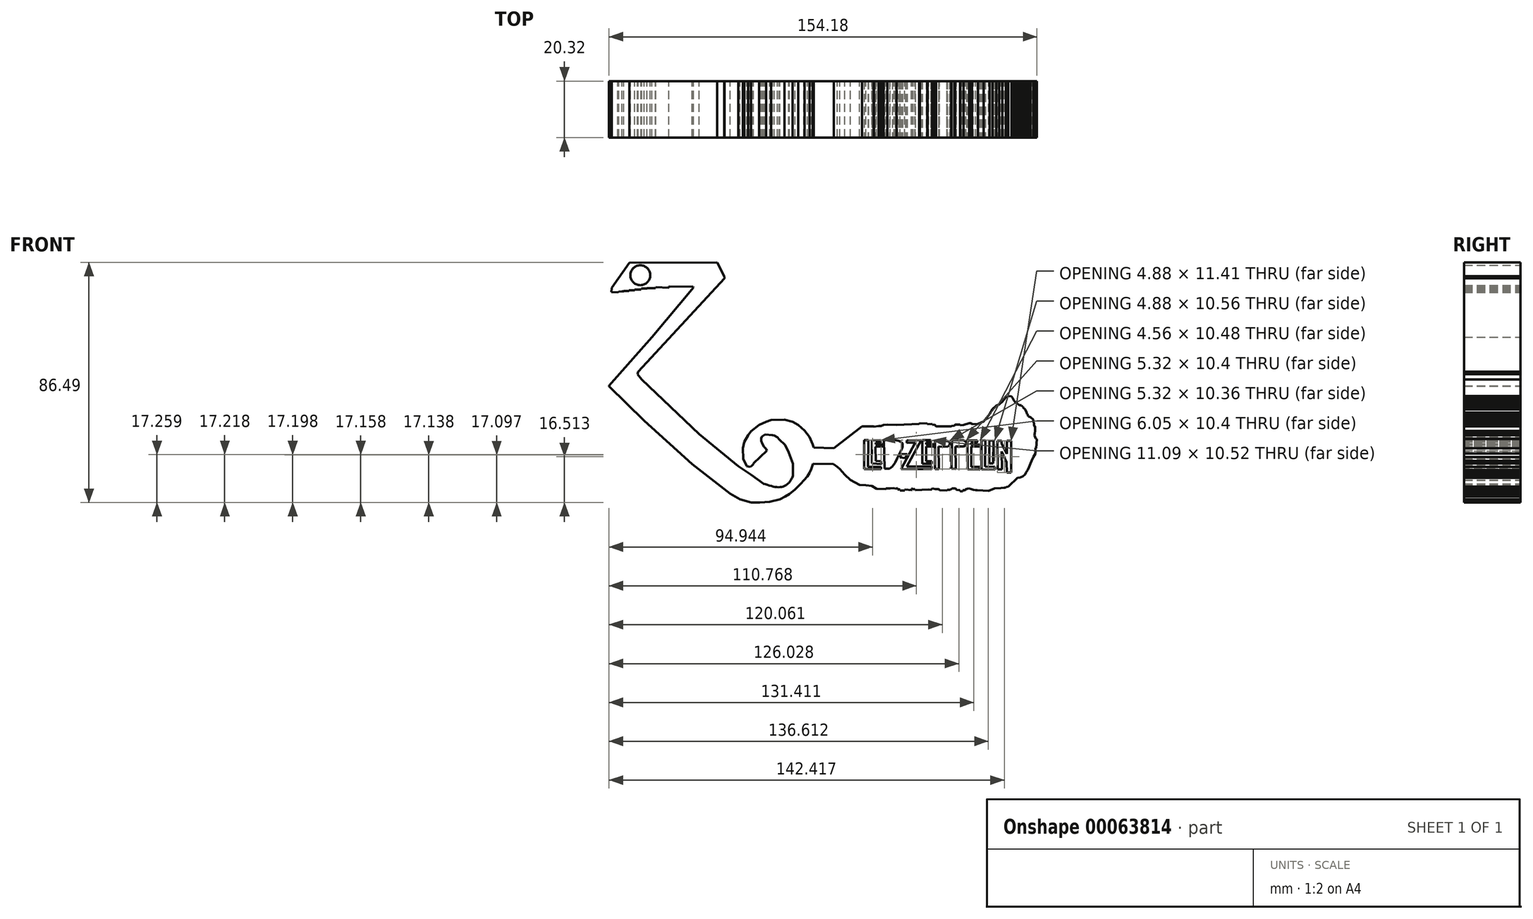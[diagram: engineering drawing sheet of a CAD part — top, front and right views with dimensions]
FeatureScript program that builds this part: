
annotation { "Feature Type Name" : "Feature", "Feature Type Description" : "" }
export const myFeature = defineFeature(function(context is Context, id is Id, definition is map)
    precondition{}
    {
        {
            var Q0;
            Q0=qCreatedBy(makeId("Front.planeOp"),FACE);
            var sketch = newSketch(context, id + "F0", { "sketchPlane" : qUnion([Q0])});
            skLineSegment(sketch, "E0", {"start": v(-87.17, 53.85) * mm, "end": v(-47.68, 54.06) * mm});
            skLineSegment(sketch, "E1", {"start": v(-47.68, 54.06) * mm, "end": v(-44.47, 47.79) * mm});
            skLineSegment(sketch, "E2", {"start": v(-44.47, 47.79) * mm, "end": v(-44.33, 46.86) * mm});
            skLineSegment(sketch, "E3", {"start": v(-44.33, 46.86) * mm, "end": v(-83.17, 4.81) * mm});
            skLineSegment(sketch, "E4", {"start": v(-83.17, 4.81) * mm, "end": v(-83.6, 3.74) * mm});
            skLineSegment(sketch, "E5", {"start": v(-83.6, 3.74) * mm, "end": v(-81.6, 1.39) * mm});
            skLineSegment(sketch, "E6", {"start": v(-81.6, 1.39) * mm, "end": v(-55.8, -23.34) * mm});
            skLineSegment(sketch, "E7", {"start": v(-55.8, -23.34) * mm, "end": v(-38.13, -37.67) * mm});
            skLineSegment(sketch, "E8", {"start": v(-38.13, -37.67) * mm, "end": v(-32.5, -41.52) * mm});
            skLineSegment(sketch, "E9", {"start": v(-32.5, -41.52) * mm, "end": v(-26.73, -45.58) * mm});
            skLineSegment(sketch, "E10", {"start": v(-13.61, -36.67) * mm, "end": v(-15.4, -31.47) * mm});
            skLineSegment(sketch, "E11", {"start": v(-19.67, -25.7) * mm, "end": v(-20.6, -24.77) * mm});
            skLineSegment(sketch, "E12", {"start": v(-20.6, -24.77) * mm, "end": v(-21.95, -23.91) * mm});
            skLineSegment(sketch, "E13", {"start": v(-21.95, -23.91) * mm, "end": v(-22.74, -23.7) * mm});
            skLineSegment(sketch, "E14", {"start": v(-22.74, -23.7) * mm, "end": v(-26.16, -23.41) * mm});
            skLineSegment(sketch, "E15", {"start": v(-26.16, -23.41) * mm, "end": v(-27.44, -24.34) * mm});
            skLineSegment(sketch, "E16", {"start": v(-27.44, -24.34) * mm, "end": v(-27.8, -25.12) * mm});
            skLineSegment(sketch, "E17", {"start": v(-27.8, -25.12) * mm, "end": v(-27.87, -26.33) * mm});
            skLineSegment(sketch, "E18", {"start": v(-27.87, -26.33) * mm, "end": v(-27.37, -27.62) * mm});
            skLineSegment(sketch, "E19", {"start": v(-27.37, -27.62) * mm, "end": v(-26.58, -28.9) * mm});
            skLineSegment(sketch, "E20", {"start": v(-26.58, -28.9) * mm, "end": v(-25.59, -29.9) * mm});
            skLineSegment(sketch, "E21", {"start": v(-25.59, -29.9) * mm, "end": v(-25.23, -30.75) * mm});
            skLineSegment(sketch, "E22", {"start": v(-25.23, -30.75) * mm, "end": v(-31.29, -36.38) * mm});
            skLineSegment(sketch, "E23", {"start": v(-31.29, -36.38) * mm, "end": v(-31.36, -36.81) * mm});
            skLineSegment(sketch, "E24", {"start": v(-31.36, -36.81) * mm, "end": v(-32, -37.45) * mm});
            skLineSegment(sketch, "E25", {"start": v(-32, -37.45) * mm, "end": v(-32.79, -37.95) * mm});
            skLineSegment(sketch, "E26", {"start": v(-32.79, -37.95) * mm, "end": v(-34.28, -37.67) * mm});
            skLineSegment(sketch, "E27", {"start": v(-34.28, -37.67) * mm, "end": v(-35.85, -34.32) * mm});
            skLineSegment(sketch, "E28", {"start": v(-35.85, -34.32) * mm, "end": v(-36.06, -29.68) * mm});
            skLineSegment(sketch, "E29", {"start": v(-36.06, -29.68) * mm, "end": v(-35.5, -26.83) * mm});
            skLineSegment(sketch, "E30", {"start": v(-35.5, -26.83) * mm, "end": v(-33.78, -23.77) * mm});
            skLineSegment(sketch, "E31", {"start": v(-33.78, -23.77) * mm, "end": v(-32.5, -22.06) * mm});
            skLineSegment(sketch, "E32", {"start": v(-32.5, -22.06) * mm, "end": v(-28.8, -19.07) * mm});
            skLineSegment(sketch, "E33", {"start": v(-28.8, -19.07) * mm, "end": v(-25.66, -17.64) * mm});
            skLineSegment(sketch, "E34", {"start": v(-25.66, -17.64) * mm, "end": v(-23.38, -16.86) * mm});
            skLineSegment(sketch, "E35", {"start": v(-23.38, -16.86) * mm, "end": v(-17.32, -16.71) * mm});
            skLineSegment(sketch, "E36", {"start": v(-17.32, -16.71) * mm, "end": v(-13.68, -17.78) * mm});
            skLineSegment(sketch, "E37", {"start": v(-13.68, -17.78) * mm, "end": v(-11.12, -19.2) * mm});
            skLineSegment(sketch, "E38", {"start": v(-11.12, -19.2) * mm, "end": v(-8.34, -21.63) * mm});
            skLineSegment(sketch, "E39", {"start": v(-8.34, -21.63) * mm, "end": v(-6.06, -24.55) * mm});
            skLineSegment(sketch, "E40", {"start": v(-6.06, -24.55) * mm, "end": v(-4.7, -27.83) * mm});
            skLineSegment(sketch, "E41", {"start": v(-4.7, -27.83) * mm, "end": v(-4.2, -29.33) * mm});
            skLineSegment(sketch, "E42", {"start": v(-4.2, -29.33) * mm, "end": v(4.92, -29.54) * mm});
            skLineSegment(sketch, "E43", {"start": v(4.92, -29.54) * mm, "end": v(17.53, -19.7) * mm});
            skLineSegment(sketch, "E44", {"start": v(17.53, -19.7) * mm, "end": v(22.88, -19.7) * mm});
            skLineSegment(sketch, "E45", {"start": v(22.88, -19.7) * mm, "end": v(23.02, -19.92) * mm});
            skLineSegment(sketch, "E46", {"start": v(23.02, -19.92) * mm, "end": v(25.02, -19.56) * mm});
            skLineSegment(sketch, "E47", {"start": v(25.02, -19.56) * mm, "end": v(26.09, -19.64) * mm});
            skLineSegment(sketch, "E48", {"start": v(26.09, -19.64) * mm, "end": v(27.3, -19.2) * mm});
            skLineSegment(sketch, "E49", {"start": v(27.3, -19.2) * mm, "end": v(28.94, -19) * mm});
            skLineSegment(sketch, "E50", {"start": v(28.94, -19) * mm, "end": v(33.07, -19.07) * mm});
            skLineSegment(sketch, "E51", {"start": v(33.07, -19.07) * mm, "end": v(43.33, -18.64) * mm});
            skLineSegment(sketch, "E52", {"start": v(43.33, -18.64) * mm, "end": v(43.62, -18.35) * mm});
            skLineSegment(sketch, "E53", {"start": v(43.62, -18.35) * mm, "end": v(46.9, -18.42) * mm});
            skLineSegment(sketch, "E54", {"start": v(46.9, -18.42) * mm, "end": v(47.11, -18.78) * mm});
            skLineSegment(sketch, "E55", {"start": v(47.11, -18.78) * mm, "end": v(49.18, -18.64) * mm});
            skLineSegment(sketch, "E56", {"start": v(49.18, -18.64) * mm, "end": v(49.32, -19.07) * mm});
            skLineSegment(sketch, "E57", {"start": v(49.32, -19.07) * mm, "end": v(50.25, -19) * mm});
            skLineSegment(sketch, "E58", {"start": v(50.25, -19) * mm, "end": v(50.96, -19.7) * mm});
            skLineSegment(sketch, "E59", {"start": v(50.96, -19.7) * mm, "end": v(57.8, -19.7) * mm});
            skLineSegment(sketch, "E60", {"start": v(57.8, -19.7) * mm, "end": v(57.94, -19.64) * mm});
            skLineSegment(sketch, "E61", {"start": v(57.94, -19.64) * mm, "end": v(59.23, -19.42) * mm});
            skLineSegment(sketch, "E62", {"start": v(59.23, -19.42) * mm, "end": v(59.51, -18.92) * mm});
            skLineSegment(sketch, "E63", {"start": v(59.51, -18.92) * mm, "end": v(61.65, -19) * mm});
            skLineSegment(sketch, "E64", {"start": v(61.65, -19) * mm, "end": v(61.94, -19.28) * mm});
            skLineSegment(sketch, "E65", {"start": v(61.94, -19.28) * mm, "end": v(63.29, -19.14) * mm});
            skLineSegment(sketch, "E66", {"start": v(63.29, -19.14) * mm, "end": v(65.78, -18.35) * mm});
            skLineSegment(sketch, "E67", {"start": v(65.78, -18.35) * mm, "end": v(66.85, -18.28) * mm});
            skLineSegment(sketch, "E68", {"start": v(66.85, -18.28) * mm, "end": v(67.07, -18.78) * mm});
            skLineSegment(sketch, "E69", {"start": v(67.07, -18.78) * mm, "end": v(69.78, -18.64) * mm});
            skLineSegment(sketch, "E70", {"start": v(69.78, -18.64) * mm, "end": v(72.34, -17.57) * mm});
            skLineSegment(sketch, "E71", {"start": v(72.34, -17.57) * mm, "end": v(75.05, -14.22) * mm});
            skLineSegment(sketch, "E72", {"start": v(75.05, -14.22) * mm, "end": v(76.26, -12) * mm});
            skLineSegment(sketch, "E73", {"start": v(76.26, -12) * mm, "end": v(78.11, -10.44) * mm});
            skLineSegment(sketch, "E74", {"start": v(78.11, -10.44) * mm, "end": v(79.4, -9.94) * mm});
            skLineSegment(sketch, "E75", {"start": v(79.4, -9.94) * mm, "end": v(80.68, -8.73) * mm});
            skLineSegment(sketch, "E76", {"start": v(80.68, -8.73) * mm, "end": v(82.4, -6.8) * mm});
            skLineSegment(sketch, "E77", {"start": v(82.4, -6.8) * mm, "end": v(83.03, -6.6) * mm});
            skLineSegment(sketch, "E78", {"start": v(83.03, -6.6) * mm, "end": v(83.46, -6.17) * mm});
            skLineSegment(sketch, "E79", {"start": v(83.46, -6.17) * mm, "end": v(84.81, -6.24) * mm});
            skLineSegment(sketch, "E80", {"start": v(84.81, -6.24) * mm, "end": v(85.31, -6.95) * mm});
            skLineSegment(sketch, "E81", {"start": v(85.31, -6.95) * mm, "end": v(85.74, -7.52) * mm});
            skLineSegment(sketch, "E82", {"start": v(85.74, -7.52) * mm, "end": v(85.95, -8.23) * mm});
            skLineSegment(sketch, "E83", {"start": v(85.95, -8.23) * mm, "end": v(86.45, -8.87) * mm});
            skLineSegment(sketch, "E84", {"start": v(86.45, -8.87) * mm, "end": v(87.24, -9.37) * mm});
            skLineSegment(sketch, "E85", {"start": v(87.24, -9.37) * mm, "end": v(88.38, -10.3) * mm});
            skLineSegment(sketch, "E86", {"start": v(88.38, -10.3) * mm, "end": v(89.3, -10.3) * mm});
            skLineSegment(sketch, "E87", {"start": v(89.3, -10.3) * mm, "end": v(89.59, -10.87) * mm});
            skLineSegment(sketch, "E88", {"start": v(89.59, -10.87) * mm, "end": v(90.09, -10.87) * mm});
            skLineSegment(sketch, "E89", {"start": v(90.09, -10.87) * mm, "end": v(90.16, -11.37) * mm});
            skLineSegment(sketch, "E90", {"start": v(90.16, -11.37) * mm, "end": v(91.01, -12.22) * mm});
            skLineSegment(sketch, "E91", {"start": v(91.01, -12.22) * mm, "end": v(91.51, -13.22) * mm});
            skLineSegment(sketch, "E92", {"start": v(91.51, -13.22) * mm, "end": v(91.73, -13.65) * mm});
            skLineSegment(sketch, "E93", {"start": v(91.73, -13.65) * mm, "end": v(91.8, -14.29) * mm});
            skLineSegment(sketch, "E94", {"start": v(91.8, -14.29) * mm, "end": v(92.15, -14.29) * mm});
            skLineSegment(sketch, "E95", {"start": v(92.15, -14.29) * mm, "end": v(92.15, -14.65) * mm});
            skLineSegment(sketch, "E96", {"start": v(92.15, -14.65) * mm, "end": v(92.44, -15.36) * mm});
            skLineSegment(sketch, "E97", {"start": v(94.65, -16.71) * mm, "end": v(94.8, -17.71) * mm});
            skLineSegment(sketch, "E98", {"start": v(94.8, -17.71) * mm, "end": v(95.08, -18.35) * mm});
            skLineSegment(sketch, "E99", {"start": v(95.08, -18.35) * mm, "end": v(95.08, -19.07) * mm});
            skLineSegment(sketch, "E100", {"start": v(95.08, -19.07) * mm, "end": v(95.3, -20) * mm});
            skLineSegment(sketch, "E101", {"start": v(95.3, -20) * mm, "end": v(95.58, -19.85) * mm});
            skLineSegment(sketch, "E102", {"start": v(95.58, -19.85) * mm, "end": v(95.5, -21.77) * mm});
            skLineSegment(sketch, "E103", {"start": v(95.5, -21.77) * mm, "end": v(95.36, -22.99) * mm});
            skLineSegment(sketch, "E104", {"start": v(95.36, -22.99) * mm, "end": v(95.22, -23.7) * mm});
            skLineSegment(sketch, "E105", {"start": v(95.22, -23.7) * mm, "end": v(95.79, -25.34) * mm});
            skLineSegment(sketch, "E106", {"start": v(95.79, -25.34) * mm, "end": v(96.36, -25.55) * mm});
            skLineSegment(sketch, "E107", {"start": v(96.36, -25.55) * mm, "end": v(96, -29.68) * mm});
            skLineSegment(sketch, "E108", {"start": v(96, -29.68) * mm, "end": v(95.65, -29.47) * mm});
            skLineSegment(sketch, "E109", {"start": v(95.65, -29.47) * mm, "end": v(95.65, -32.04) * mm});
            skLineSegment(sketch, "E110", {"start": v(95.65, -32.04) * mm, "end": v(94.8, -33.6) * mm});
            skLineSegment(sketch, "E111", {"start": v(94.8, -33.6) * mm, "end": v(93.94, -35.32) * mm});
            skLineSegment(sketch, "E112", {"start": v(93.94, -35.32) * mm, "end": v(93.44, -36.38) * mm});
            skLineSegment(sketch, "E113", {"start": v(93.44, -36.38) * mm, "end": v(92.87, -38.02) * mm});
            skLineSegment(sketch, "E114", {"start": v(92.87, -38.02) * mm, "end": v(92.15, -39.45) * mm});
            skLineSegment(sketch, "E115", {"start": v(92.15, -39.45) * mm, "end": v(91.37, -40.59) * mm});
            skLineSegment(sketch, "E116", {"start": v(91.37, -40.59) * mm, "end": v(91.01, -41.3) * mm});
            skLineSegment(sketch, "E117", {"start": v(91.01, -41.3) * mm, "end": v(90.02, -42.3) * mm});
            skLineSegment(sketch, "E118", {"start": v(90.02, -42.3) * mm, "end": v(88.3, -43.01) * mm});
            skLineSegment(sketch, "E119", {"start": v(88.3, -43.01) * mm, "end": v(87.66, -42.73) * mm});
            skLineSegment(sketch, "E120", {"start": v(87.66, -42.73) * mm, "end": v(83.39, -46.93) * mm});
            skLineSegment(sketch, "E121", {"start": v(83.39, -46.93) * mm, "end": v(82.46, -47.08) * mm});
            skLineSegment(sketch, "E122", {"start": v(82.46, -47.08) * mm, "end": v(82.18, -47.36) * mm});
            skLineSegment(sketch, "E123", {"start": v(82.18, -47.36) * mm, "end": v(81.6, -47.36) * mm});
            skLineSegment(sketch, "E124", {"start": v(81.6, -47.36) * mm, "end": v(80.18, -47.5) * mm});
            skLineSegment(sketch, "E125", {"start": v(80.18, -47.5) * mm, "end": v(77.26, -47.65) * mm});
            skLineSegment(sketch, "E126", {"start": v(77.26, -47.65) * mm, "end": v(74.55, -48.79) * mm});
            skLineSegment(sketch, "E127", {"start": v(74.55, -48.79) * mm, "end": v(69.42, -48.57) * mm});
            skLineSegment(sketch, "E128", {"start": v(69.42, -48.57) * mm, "end": v(68.7, -48.57) * mm});
            skLineSegment(sketch, "E129", {"start": v(68.7, -48.57) * mm, "end": v(67.7, -48.29) * mm});
            skLineSegment(sketch, "E130", {"start": v(67.7, -48.29) * mm, "end": v(66.85, -48) * mm});
            skLineSegment(sketch, "E131", {"start": v(66.85, -48) * mm, "end": v(65.71, -47.79) * mm});
            skLineSegment(sketch, "E132", {"start": v(64.43, -48.07) * mm, "end": v(64.07, -48.5) * mm});
            skLineSegment(sketch, "E133", {"start": v(64.07, -48.5) * mm, "end": v(63, -48.43) * mm});
            skLineSegment(sketch, "E134", {"start": v(63, -48.43) * mm, "end": v(62.86, -49.07) * mm});
            skLineSegment(sketch, "E135", {"start": v(62.86, -49.07) * mm, "end": v(61.65, -49) * mm});
            skLineSegment(sketch, "E136", {"start": v(61.65, -49) * mm, "end": v(61.65, -48.5) * mm});
            skLineSegment(sketch, "E137", {"start": v(61.65, -48.5) * mm, "end": v(60.15, -48.36) * mm});
            skLineSegment(sketch, "E138", {"start": v(60.15, -48.36) * mm, "end": v(59.73, -47.93) * mm});
            skLineSegment(sketch, "E139", {"start": v(59.73, -47.93) * mm, "end": v(59.37, -47.72) * mm});
            skLineSegment(sketch, "E140", {"start": v(59.37, -47.72) * mm, "end": v(58.02, -47.72) * mm});
            skLineSegment(sketch, "E141", {"start": v(58.02, -47.72) * mm, "end": v(57.87, -48.07) * mm});
            skLineSegment(sketch, "E142", {"start": v(57.87, -48.07) * mm, "end": v(57.66, -48.07) * mm});
            skLineSegment(sketch, "E143", {"start": v(57.66, -48.07) * mm, "end": v(57.3, -48.29) * mm});
            skLineSegment(sketch, "E144", {"start": v(57.3, -48.29) * mm, "end": v(56.02, -48.29) * mm});
            skLineSegment(sketch, "E145", {"start": v(56.02, -48.29) * mm, "end": v(55.88, -48.71) * mm});
            skLineSegment(sketch, "E146", {"start": v(55.88, -48.71) * mm, "end": v(52.46, -48.5) * mm});
            skLineSegment(sketch, "E147", {"start": v(52.46, -48.5) * mm, "end": v(52.17, -48.07) * mm});
            skLineSegment(sketch, "E148", {"start": v(52.17, -48.07) * mm, "end": v(50.53, -48.07) * mm});
            skLineSegment(sketch, "E149", {"start": v(50.53, -48.07) * mm, "end": v(49.1, -47.72) * mm});
            skLineSegment(sketch, "E150", {"start": v(49.1, -47.72) * mm, "end": v(48.75, -48.29) * mm});
            skLineSegment(sketch, "E151", {"start": v(48.75, -48.29) * mm, "end": v(47.6, -48.22) * mm});
            skLineSegment(sketch, "E152", {"start": v(47.6, -48.22) * mm, "end": v(41.55, -48.5) * mm});
            skLineSegment(sketch, "E153", {"start": v(41.55, -48.5) * mm, "end": v(41.34, -48.07) * mm});
            skLineSegment(sketch, "E154", {"start": v(41.34, -48.07) * mm, "end": v(40.62, -48.07) * mm});
            skLineSegment(sketch, "E155", {"start": v(40.62, -48.07) * mm, "end": v(39.84, -47.65) * mm});
            skLineSegment(sketch, "E156", {"start": v(40.05, -48.43) * mm, "end": v(36.85, -48.14) * mm});
            skLineSegment(sketch, "E157", {"start": v(36.85, -48.14) * mm, "end": v(36.85, -48.71) * mm});
            skLineSegment(sketch, "E158", {"start": v(36.85, -48.71) * mm, "end": v(34.64, -48.71) * mm});
            skLineSegment(sketch, "E159", {"start": v(34.64, -48.71) * mm, "end": v(34.64, -48.14) * mm});
            skLineSegment(sketch, "E160", {"start": v(34.64, -48.14) * mm, "end": v(33.64, -48.14) * mm});
            skLineSegment(sketch, "E161", {"start": v(33.64, -48.14) * mm, "end": v(33.57, -47.57) * mm});
            skLineSegment(sketch, "E162", {"start": v(33.57, -47.57) * mm, "end": v(32.43, -47.93) * mm});
            skLineSegment(sketch, "E163", {"start": v(32.43, -47.93) * mm, "end": v(32, -47.5) * mm});
            skLineSegment(sketch, "E164", {"start": v(32, -47.5) * mm, "end": v(30.22, -47.65) * mm});
            skLineSegment(sketch, "E165", {"start": v(30.22, -47.65) * mm, "end": v(28.44, -47.65) * mm});
            skLineSegment(sketch, "E166", {"start": v(28.44, -47.65) * mm, "end": v(28.37, -48) * mm});
            skLineSegment(sketch, "E167", {"start": v(28.37, -48) * mm, "end": v(24.09, -47.86) * mm});
            skLineSegment(sketch, "E168", {"start": v(12.4, -43.94) * mm, "end": v(9.84, -41.44) * mm});
            skLineSegment(sketch, "E169", {"start": v(9.84, -41.44) * mm, "end": v(7.55, -39.02) * mm});
            skLineSegment(sketch, "E170", {"start": v(7.55, -39.02) * mm, "end": v(6.41, -38.02) * mm});
            skLineSegment(sketch, "E171", {"start": v(6.41, -38.02) * mm, "end": v(4.78, -36.81) * mm});
            skLineSegment(sketch, "E172", {"start": v(4.78, -36.81) * mm, "end": v(-4.5, -36.53) * mm});
            skLineSegment(sketch, "E173", {"start": v(-4.5, -36.53) * mm, "end": v(-5.35, -38.95) * mm});
            skLineSegment(sketch, "E174", {"start": v(-5.35, -38.95) * mm, "end": v(-6.06, -40.73) * mm});
            skLineSegment(sketch, "E175", {"start": v(-6.06, -40.73) * mm, "end": v(-7.06, -42.3) * mm});
            skLineSegment(sketch, "E176", {"start": v(-7.06, -42.3) * mm, "end": v(-8.62, -44.08) * mm});
            skLineSegment(sketch, "E177", {"start": v(-8.62, -44.08) * mm, "end": v(-10.12, -45.65) * mm});
            skLineSegment(sketch, "E178", {"start": v(-10.12, -45.65) * mm, "end": v(-12.62, -48.22) * mm});
            skLineSegment(sketch, "E179", {"start": v(-12.62, -48.22) * mm, "end": v(-15.1, -50.21) * mm});
            skLineSegment(sketch, "E180", {"start": v(-15.1, -50.21) * mm, "end": v(-17.1, -51.42) * mm});
            skLineSegment(sketch, "E181", {"start": v(-17.1, -51.42) * mm, "end": v(-19.46, -52.63) * mm});
            skLineSegment(sketch, "E182", {"start": v(-28.44, -54.06) * mm, "end": v(-32.29, -53.99) * mm});
            skLineSegment(sketch, "E183", {"start": v(-32.29, -53.99) * mm, "end": v(-37.35, -52.63) * mm});
            skLineSegment(sketch, "E184", {"start": v(-37.35, -52.63) * mm, "end": v(-41.84, -50.07) * mm});
            skLineSegment(sketch, "E185", {"start": v(-41.84, -50.07) * mm, "end": v(-59.01, -36.74) * mm});
            skLineSegment(sketch, "E186", {"start": v(-59.01, -36.74) * mm, "end": v(-80.54, -17.21) * mm});
            skLineSegment(sketch, "E187", {"start": v(-80.54, -17.21) * mm, "end": v(-96.36, -1.75) * mm});
            skLineSegment(sketch, "E188", {"start": v(-96.36, -1.75) * mm, "end": v(-96.36, -1.46) * mm});
            skLineSegment(sketch, "E189", {"start": v(-96.36, -1.46) * mm, "end": v(-76.97, 20.35) * mm});
            skLineSegment(sketch, "E190", {"start": v(-76.97, 20.35) * mm, "end": v(-58.3, 42.73) * mm});
            skLineSegment(sketch, "E191", {"start": v(-58.3, 42.73) * mm, "end": v(-58.44, 43.08) * mm});
            skLineSegment(sketch, "E192", {"start": v(-58.44, 43.08) * mm, "end": v(-69.35, 43.3) * mm});
            skLineSegment(sketch, "E193", {"start": v(-69.35, 43.3) * mm, "end": v(-69.42, 42.66) * mm});
            skLineSegment(sketch, "E194", {"start": v(-69.42, 42.66) * mm, "end": v(-75.26, 42.94) * mm});
            skLineSegment(sketch, "E195", {"start": v(-81.82, 42.23) * mm, "end": v(-82.03, 41.8) * mm});
            skLineSegment(sketch, "E196", {"start": v(-82.03, 41.8) * mm, "end": v(-84.81, 41.8) * mm});
            skLineSegment(sketch, "E197", {"start": v(-84.81, 41.8) * mm, "end": v(-84.81, 41.52) * mm});
            skLineSegment(sketch, "E198", {"start": v(-84.81, 41.52) * mm, "end": v(-87.3, 41.44) * mm});
            skLineSegment(sketch, "E199", {"start": v(-87.3, 41.44) * mm, "end": v(-87.38, 41.23) * mm});
            skLineSegment(sketch, "E200", {"start": v(-87.38, 41.23) * mm, "end": v(-89.8, 41.16) * mm});
            skLineSegment(sketch, "E201", {"start": v(-89.8, 41.16) * mm, "end": v(-89.8, 41.02) * mm});
            skLineSegment(sketch, "E202", {"start": v(-89.8, 41.02) * mm, "end": v(-90.59, 41.02) * mm});
            skLineSegment(sketch, "E203", {"start": v(-90.59, 41.02) * mm, "end": v(-91.94, 40.87) * mm});
            skLineSegment(sketch, "E204", {"start": v(-91.94, 40.87) * mm, "end": v(-92.44, 40.59) * mm});
            skLineSegment(sketch, "E205", {"start": v(-92.44, 40.59) * mm, "end": v(-95.36, 40.73) * mm});
            skLineSegment(sketch, "E206", {"start": v(-95.36, 40.73) * mm, "end": v(-95.08, 42.66) * mm});
            skLineSegment(sketch, "E207", {"start": v(-79.18, 42.51) * mm, "end": v(-75.4, 42.44) * mm});
            skLineSegment(sketch, "E208", {"start": v(-75.4, 42.44) * mm, "end": v(-75.26, 42.94) * mm});
            skLineSegment(sketch, "E209", {"start": v(-79.18, 42.23) * mm, "end": v(-79.18, 42.51) * mm});
            skLineSegment(sketch, "E210", {"start": v(-81.82, 42.23) * mm, "end": v(-79.18, 42.23) * mm});
            skLineSegment(sketch, "E211", {"start": v(-17.1, -28.19) * mm, "end": v(-15.4, -31.47) * mm});
            skLineSegment(sketch, "E212", {"start": v(-19.67, -25.7) * mm, "end": v(-17.1, -28.19) * mm});
            skLineSegment(sketch, "E213", {"start": v(-13.61, -36.67) * mm, "end": v(-13.61, -42.01) * mm});
            skFitSpline(sketch, "E214", {"points": [v(-26.73, -45.58) * mm, v(-18.74, -47.08) * mm, v(-14.82, -44.58) * mm, v(-13.61, -42.01) * mm], "startDerivative": vector(20.1, -6.72) * mm, "endDerivative": vector(3.43, 10.2) * mm});
            skLineSegment(sketch, "E215", {"start": v(-24.02, -53.77) * mm, "end": v(-19.46, -52.63) * mm});
            skLineSegment(sketch, "E216", {"start": v(-95.08, 42.66) * mm, "end": v(-87.17, 53.85) * mm});
            skLineSegment(sketch, "E217", {"start": v(39.84, -47.65) * mm, "end": v(40.05, -48.43) * mm});
            skLineSegment(sketch, "E218", {"start": v(-28.44, -54.06) * mm, "end": v(-24.02, -53.77) * mm});
            skLineSegment(sketch, "E219", {"start": v(12.4, -43.94) * mm, "end": v(16.46, -46.15) * mm});
            skLineSegment(sketch, "E220", {"start": v(19.31, -46.22) * mm, "end": v(16.46, -46.15) * mm});
            skLineSegment(sketch, "E221", {"start": v(19.31, -46.22) * mm, "end": v(22.02, -46.58) * mm});
            skLineSegment(sketch, "E222", {"start": v(24.09, -47.86) * mm, "end": v(22.02, -46.58) * mm});
            skLineSegment(sketch, "E223", {"start": v(64.43, -48.07) * mm, "end": v(65.71, -47.79) * mm});
            skLineSegment(sketch, "E224", {"start": v(92.44, -15.36) * mm, "end": v(93.53, -15.67) * mm});
            skLineSegment(sketch, "E225", {"start": v(93.53, -15.67) * mm, "end": v(94.65, -16.71) * mm});
            skSolve(sketch);
        }
        {
            var Q0;
            Q0=makeQuery(id+"F0.imprint","IMPRINT",FACE,{"disambiguationData":[TD([[makeQuery(id+"F0.imprint","IMPRINT",EDGE,{"derivedFrom":sQuery(id+"F0.wireOp",EDGE,"E0")}),-1.0]])]});
            extrude(context, id + "F1", {"entities" : qUnion([Q0]), "depth" : 25.4 * mm});
        }
        {
            var Q0;
            Q0=makeQuery(id+"F1.opExtrude","SWEPT_BODY",BODY,{"disambiguationData":[OSD([sQuery(id+"F0.wireOp",EDGE,"E0"),sQuery(id+"F0.wireOp",EDGE,"E1"),sQuery(id+"F0.wireOp",EDGE,"E2"),sQuery(id+"F0.wireOp",EDGE,"E3"),sQuery(id+"F0.wireOp",EDGE,"E4"),sQuery(id+"F0.wireOp",EDGE,"E5"),sQuery(id+"F0.wireOp",EDGE,"E6"),sQuery(id+"F0.wireOp",EDGE,"E7"),sQuery(id+"F0.wireOp",EDGE,"E8"),sQuery(id+"F0.wireOp",EDGE,"E9"),sQuery(id+"F0.wireOp",EDGE,"E10"),sQuery(id+"F0.wireOp",EDGE,"E11"),sQuery(id+"F0.wireOp",EDGE,"E12"),sQuery(id+"F0.wireOp",EDGE,"E13"),sQuery(id+"F0.wireOp",EDGE,"E14"),sQuery(id+"F0.wireOp",EDGE,"E15"),sQuery(id+"F0.wireOp",EDGE,"E16"),sQuery(id+"F0.wireOp",EDGE,"E17"),sQuery(id+"F0.wireOp",EDGE,"E18"),sQuery(id+"F0.wireOp",EDGE,"E19"),sQuery(id+"F0.wireOp",EDGE,"E20"),sQuery(id+"F0.wireOp",EDGE,"E21"),sQuery(id+"F0.wireOp",EDGE,"E22"),sQuery(id+"F0.wireOp",EDGE,"E23"),sQuery(id+"F0.wireOp",EDGE,"E24"),sQuery(id+"F0.wireOp",EDGE,"E25"),sQuery(id+"F0.wireOp",EDGE,"E26"),sQuery(id+"F0.wireOp",EDGE,"E27"),sQuery(id+"F0.wireOp",EDGE,"E28"),sQuery(id+"F0.wireOp",EDGE,"E29"),sQuery(id+"F0.wireOp",EDGE,"E30"),sQuery(id+"F0.wireOp",EDGE,"E31"),sQuery(id+"F0.wireOp",EDGE,"E32"),sQuery(id+"F0.wireOp",EDGE,"E33"),sQuery(id+"F0.wireOp",EDGE,"E34"),sQuery(id+"F0.wireOp",EDGE,"E35"),sQuery(id+"F0.wireOp",EDGE,"E36"),sQuery(id+"F0.wireOp",EDGE,"E37"),sQuery(id+"F0.wireOp",EDGE,"E38"),sQuery(id+"F0.wireOp",EDGE,"E39"),sQuery(id+"F0.wireOp",EDGE,"E40"),sQuery(id+"F0.wireOp",EDGE,"E41"),sQuery(id+"F0.wireOp",EDGE,"E42"),sQuery(id+"F0.wireOp",EDGE,"E43"),sQuery(id+"F0.wireOp",EDGE,"E44"),sQuery(id+"F0.wireOp",EDGE,"E45"),sQuery(id+"F0.wireOp",EDGE,"E46"),sQuery(id+"F0.wireOp",EDGE,"E47"),sQuery(id+"F0.wireOp",EDGE,"E48"),sQuery(id+"F0.wireOp",EDGE,"E49"),sQuery(id+"F0.wireOp",EDGE,"E50"),sQuery(id+"F0.wireOp",EDGE,"E51"),sQuery(id+"F0.wireOp",EDGE,"E52"),sQuery(id+"F0.wireOp",EDGE,"E53"),sQuery(id+"F0.wireOp",EDGE,"E54"),sQuery(id+"F0.wireOp",EDGE,"E55"),sQuery(id+"F0.wireOp",EDGE,"E56"),sQuery(id+"F0.wireOp",EDGE,"E57"),sQuery(id+"F0.wireOp",EDGE,"E58"),sQuery(id+"F0.wireOp",EDGE,"E59"),sQuery(id+"F0.wireOp",EDGE,"E60"),sQuery(id+"F0.wireOp",EDGE,"E61"),sQuery(id+"F0.wireOp",EDGE,"E62"),sQuery(id+"F0.wireOp",EDGE,"E63"),sQuery(id+"F0.wireOp",EDGE,"E64"),sQuery(id+"F0.wireOp",EDGE,"E65"),sQuery(id+"F0.wireOp",EDGE,"E66"),sQuery(id+"F0.wireOp",EDGE,"E67"),sQuery(id+"F0.wireOp",EDGE,"E68"),sQuery(id+"F0.wireOp",EDGE,"E69"),sQuery(id+"F0.wireOp",EDGE,"E70"),sQuery(id+"F0.wireOp",EDGE,"E71"),sQuery(id+"F0.wireOp",EDGE,"E72"),sQuery(id+"F0.wireOp",EDGE,"E73"),sQuery(id+"F0.wireOp",EDGE,"E74"),sQuery(id+"F0.wireOp",EDGE,"E75"),sQuery(id+"F0.wireOp",EDGE,"E76"),sQuery(id+"F0.wireOp",EDGE,"E77"),sQuery(id+"F0.wireOp",EDGE,"E78"),sQuery(id+"F0.wireOp",EDGE,"E79"),sQuery(id+"F0.wireOp",EDGE,"E80"),sQuery(id+"F0.wireOp",EDGE,"E81"),sQuery(id+"F0.wireOp",EDGE,"E82"),sQuery(id+"F0.wireOp",EDGE,"E83"),sQuery(id+"F0.wireOp",EDGE,"E84"),sQuery(id+"F0.wireOp",EDGE,"E85"),sQuery(id+"F0.wireOp",EDGE,"E86"),sQuery(id+"F0.wireOp",EDGE,"E87"),sQuery(id+"F0.wireOp",EDGE,"E88"),sQuery(id+"F0.wireOp",EDGE,"E89"),sQuery(id+"F0.wireOp",EDGE,"E90"),sQuery(id+"F0.wireOp",EDGE,"E91"),sQuery(id+"F0.wireOp",EDGE,"E92"),sQuery(id+"F0.wireOp",EDGE,"E93"),sQuery(id+"F0.wireOp",EDGE,"E94"),sQuery(id+"F0.wireOp",EDGE,"E95"),sQuery(id+"F0.wireOp",EDGE,"E96"),sQuery(id+"F0.wireOp",EDGE,"E97"),sQuery(id+"F0.wireOp",EDGE,"E98"),sQuery(id+"F0.wireOp",EDGE,"E99"),sQuery(id+"F0.wireOp",EDGE,"E100"),sQuery(id+"F0.wireOp",EDGE,"E101"),sQuery(id+"F0.wireOp",EDGE,"E102"),sQuery(id+"F0.wireOp",EDGE,"E103"),sQuery(id+"F0.wireOp",EDGE,"E104"),sQuery(id+"F0.wireOp",EDGE,"E105"),sQuery(id+"F0.wireOp",EDGE,"E106"),sQuery(id+"F0.wireOp",EDGE,"E107"),sQuery(id+"F0.wireOp",EDGE,"E108"),sQuery(id+"F0.wireOp",EDGE,"E109"),sQuery(id+"F0.wireOp",EDGE,"E110"),sQuery(id+"F0.wireOp",EDGE,"E111"),sQuery(id+"F0.wireOp",EDGE,"E112"),sQuery(id+"F0.wireOp",EDGE,"E113"),sQuery(id+"F0.wireOp",EDGE,"E114"),sQuery(id+"F0.wireOp",EDGE,"E115"),sQuery(id+"F0.wireOp",EDGE,"E116"),sQuery(id+"F0.wireOp",EDGE,"E117"),sQuery(id+"F0.wireOp",EDGE,"E118"),sQuery(id+"F0.wireOp",EDGE,"E119"),sQuery(id+"F0.wireOp",EDGE,"E120"),sQuery(id+"F0.wireOp",EDGE,"E121"),sQuery(id+"F0.wireOp",EDGE,"E122"),sQuery(id+"F0.wireOp",EDGE,"E123"),sQuery(id+"F0.wireOp",EDGE,"E124"),sQuery(id+"F0.wireOp",EDGE,"E125"),sQuery(id+"F0.wireOp",EDGE,"E126"),sQuery(id+"F0.wireOp",EDGE,"E127"),sQuery(id+"F0.wireOp",EDGE,"E128"),sQuery(id+"F0.wireOp",EDGE,"E129"),sQuery(id+"F0.wireOp",EDGE,"E130"),sQuery(id+"F0.wireOp",EDGE,"E131"),sQuery(id+"F0.wireOp",EDGE,"E132"),sQuery(id+"F0.wireOp",EDGE,"E133"),sQuery(id+"F0.wireOp",EDGE,"E134"),sQuery(id+"F0.wireOp",EDGE,"E135"),sQuery(id+"F0.wireOp",EDGE,"E136"),sQuery(id+"F0.wireOp",EDGE,"E137"),sQuery(id+"F0.wireOp",EDGE,"E138"),sQuery(id+"F0.wireOp",EDGE,"E139"),sQuery(id+"F0.wireOp",EDGE,"E140"),sQuery(id+"F0.wireOp",EDGE,"E141"),sQuery(id+"F0.wireOp",EDGE,"E142"),sQuery(id+"F0.wireOp",EDGE,"E143"),sQuery(id+"F0.wireOp",EDGE,"E144"),sQuery(id+"F0.wireOp",EDGE,"E145"),sQuery(id+"F0.wireOp",EDGE,"E146"),sQuery(id+"F0.wireOp",EDGE,"E147"),sQuery(id+"F0.wireOp",EDGE,"E148"),sQuery(id+"F0.wireOp",EDGE,"E149"),sQuery(id+"F0.wireOp",EDGE,"E150"),sQuery(id+"F0.wireOp",EDGE,"E151"),sQuery(id+"F0.wireOp",EDGE,"E152"),sQuery(id+"F0.wireOp",EDGE,"E153"),sQuery(id+"F0.wireOp",EDGE,"E154"),sQuery(id+"F0.wireOp",EDGE,"E155"),sQuery(id+"F0.wireOp",EDGE,"E156"),sQuery(id+"F0.wireOp",EDGE,"E157"),sQuery(id+"F0.wireOp",EDGE,"E158"),sQuery(id+"F0.wireOp",EDGE,"E159"),sQuery(id+"F0.wireOp",EDGE,"E160"),sQuery(id+"F0.wireOp",EDGE,"E161"),sQuery(id+"F0.wireOp",EDGE,"E162"),sQuery(id+"F0.wireOp",EDGE,"E163"),sQuery(id+"F0.wireOp",EDGE,"E164"),sQuery(id+"F0.wireOp",EDGE,"E165"),sQuery(id+"F0.wireOp",EDGE,"E166"),sQuery(id+"F0.wireOp",EDGE,"E167"),sQuery(id+"F0.wireOp",EDGE,"E168"),sQuery(id+"F0.wireOp",EDGE,"E169"),sQuery(id+"F0.wireOp",EDGE,"E170"),sQuery(id+"F0.wireOp",EDGE,"E171"),sQuery(id+"F0.wireOp",EDGE,"E172"),sQuery(id+"F0.wireOp",EDGE,"E173"),sQuery(id+"F0.wireOp",EDGE,"E174"),sQuery(id+"F0.wireOp",EDGE,"E175"),sQuery(id+"F0.wireOp",EDGE,"E176"),sQuery(id+"F0.wireOp",EDGE,"E177"),sQuery(id+"F0.wireOp",EDGE,"E178"),sQuery(id+"F0.wireOp",EDGE,"E179"),sQuery(id+"F0.wireOp",EDGE,"E180"),sQuery(id+"F0.wireOp",EDGE,"E181"),sQuery(id+"F0.wireOp",EDGE,"E182"),sQuery(id+"F0.wireOp",EDGE,"E183"),sQuery(id+"F0.wireOp",EDGE,"E184"),sQuery(id+"F0.wireOp",EDGE,"E185"),sQuery(id+"F0.wireOp",EDGE,"E186"),sQuery(id+"F0.wireOp",EDGE,"E187"),sQuery(id+"F0.wireOp",EDGE,"E188"),sQuery(id+"F0.wireOp",EDGE,"E189"),sQuery(id+"F0.wireOp",EDGE,"E190"),sQuery(id+"F0.wireOp",EDGE,"E191"),sQuery(id+"F0.wireOp",EDGE,"E192"),sQuery(id+"F0.wireOp",EDGE,"E193"),sQuery(id+"F0.wireOp",EDGE,"E194"),sQuery(id+"F0.wireOp",EDGE,"E195"),sQuery(id+"F0.wireOp",EDGE,"E196"),sQuery(id+"F0.wireOp",EDGE,"E197"),sQuery(id+"F0.wireOp",EDGE,"E198"),sQuery(id+"F0.wireOp",EDGE,"E199"),sQuery(id+"F0.wireOp",EDGE,"E200"),sQuery(id+"F0.wireOp",EDGE,"E201"),sQuery(id+"F0.wireOp",EDGE,"E202"),sQuery(id+"F0.wireOp",EDGE,"E203"),sQuery(id+"F0.wireOp",EDGE,"E204"),sQuery(id+"F0.wireOp",EDGE,"E205"),sQuery(id+"F0.wireOp",EDGE,"E206"),sQuery(id+"F0.wireOp",EDGE,"E207"),sQuery(id+"F0.wireOp",EDGE,"E208"),sQuery(id+"F0.wireOp",EDGE,"E209"),sQuery(id+"F0.wireOp",EDGE,"E210"),sQuery(id+"F0.wireOp",EDGE,"E211"),sQuery(id+"F0.wireOp",EDGE,"E212"),sQuery(id+"F0.wireOp",EDGE,"E213"),sQuery(id+"F0.wireOp",EDGE,"E214"),sQuery(id+"F0.wireOp",EDGE,"E215"),sQuery(id+"F0.wireOp",EDGE,"E216"),sQuery(id+"F0.wireOp",EDGE,"E217"),sQuery(id+"F0.wireOp",EDGE,"E218"),sQuery(id+"F0.wireOp",EDGE,"E219"),sQuery(id+"F0.wireOp",EDGE,"E220"),sQuery(id+"F0.wireOp",EDGE,"E221"),sQuery(id+"F0.wireOp",EDGE,"E222"),sQuery(id+"F0.wireOp",EDGE,"E223"),sQuery(id+"F0.wireOp",EDGE,"E224"),sQuery(id+"F0.wireOp",EDGE,"E225")])]});
            var Q1;
            Q1=makeQuery(id+"F1.opExtrude","CAP_VERTEX",VERTEX,{"disambiguationData":[OSD([sQuery(id+"F0.wireOp",EDGE,"E205"),sQuery(id+"F0.wireOp",EDGE,"E206")])],"isStart":false});
            transform(context, id + "F2", {"entities" : qUnion([Q0]), "transformType" : TransformType.SCALE_UNIFORMLY, "scale" : .2, "makeCopy" : false, "scalePoint" : qUnion([Q1])});
        }
        {
            var Q0;
            Q0=makeQuery(id+"F1.opExtrude","SWEPT_BODY",BODY,{"disambiguationData":[OSD([sQuery(id+"F0.wireOp",EDGE,"E0"),sQuery(id+"F0.wireOp",EDGE,"E1"),sQuery(id+"F0.wireOp",EDGE,"E2"),sQuery(id+"F0.wireOp",EDGE,"E3"),sQuery(id+"F0.wireOp",EDGE,"E4"),sQuery(id+"F0.wireOp",EDGE,"E5"),sQuery(id+"F0.wireOp",EDGE,"E6"),sQuery(id+"F0.wireOp",EDGE,"E7"),sQuery(id+"F0.wireOp",EDGE,"E8"),sQuery(id+"F0.wireOp",EDGE,"E9"),sQuery(id+"F0.wireOp",EDGE,"E10"),sQuery(id+"F0.wireOp",EDGE,"E11"),sQuery(id+"F0.wireOp",EDGE,"E12"),sQuery(id+"F0.wireOp",EDGE,"E13"),sQuery(id+"F0.wireOp",EDGE,"E14"),sQuery(id+"F0.wireOp",EDGE,"E15"),sQuery(id+"F0.wireOp",EDGE,"E16"),sQuery(id+"F0.wireOp",EDGE,"E17"),sQuery(id+"F0.wireOp",EDGE,"E18"),sQuery(id+"F0.wireOp",EDGE,"E19"),sQuery(id+"F0.wireOp",EDGE,"E20"),sQuery(id+"F0.wireOp",EDGE,"E21"),sQuery(id+"F0.wireOp",EDGE,"E22"),sQuery(id+"F0.wireOp",EDGE,"E23"),sQuery(id+"F0.wireOp",EDGE,"E24"),sQuery(id+"F0.wireOp",EDGE,"E25"),sQuery(id+"F0.wireOp",EDGE,"E26"),sQuery(id+"F0.wireOp",EDGE,"E27"),sQuery(id+"F0.wireOp",EDGE,"E28"),sQuery(id+"F0.wireOp",EDGE,"E29"),sQuery(id+"F0.wireOp",EDGE,"E30"),sQuery(id+"F0.wireOp",EDGE,"E31"),sQuery(id+"F0.wireOp",EDGE,"E32"),sQuery(id+"F0.wireOp",EDGE,"E33"),sQuery(id+"F0.wireOp",EDGE,"E34"),sQuery(id+"F0.wireOp",EDGE,"E35"),sQuery(id+"F0.wireOp",EDGE,"E36"),sQuery(id+"F0.wireOp",EDGE,"E37"),sQuery(id+"F0.wireOp",EDGE,"E38"),sQuery(id+"F0.wireOp",EDGE,"E39"),sQuery(id+"F0.wireOp",EDGE,"E40"),sQuery(id+"F0.wireOp",EDGE,"E41"),sQuery(id+"F0.wireOp",EDGE,"E42"),sQuery(id+"F0.wireOp",EDGE,"E43"),sQuery(id+"F0.wireOp",EDGE,"E44"),sQuery(id+"F0.wireOp",EDGE,"E45"),sQuery(id+"F0.wireOp",EDGE,"E46"),sQuery(id+"F0.wireOp",EDGE,"E47"),sQuery(id+"F0.wireOp",EDGE,"E48"),sQuery(id+"F0.wireOp",EDGE,"E49"),sQuery(id+"F0.wireOp",EDGE,"E50"),sQuery(id+"F0.wireOp",EDGE,"E51"),sQuery(id+"F0.wireOp",EDGE,"E52"),sQuery(id+"F0.wireOp",EDGE,"E53"),sQuery(id+"F0.wireOp",EDGE,"E54"),sQuery(id+"F0.wireOp",EDGE,"E55"),sQuery(id+"F0.wireOp",EDGE,"E56"),sQuery(id+"F0.wireOp",EDGE,"E57"),sQuery(id+"F0.wireOp",EDGE,"E58"),sQuery(id+"F0.wireOp",EDGE,"E59"),sQuery(id+"F0.wireOp",EDGE,"E60"),sQuery(id+"F0.wireOp",EDGE,"E61"),sQuery(id+"F0.wireOp",EDGE,"E62"),sQuery(id+"F0.wireOp",EDGE,"E63"),sQuery(id+"F0.wireOp",EDGE,"E64"),sQuery(id+"F0.wireOp",EDGE,"E65"),sQuery(id+"F0.wireOp",EDGE,"E66"),sQuery(id+"F0.wireOp",EDGE,"E67"),sQuery(id+"F0.wireOp",EDGE,"E68"),sQuery(id+"F0.wireOp",EDGE,"E69"),sQuery(id+"F0.wireOp",EDGE,"E70"),sQuery(id+"F0.wireOp",EDGE,"E71"),sQuery(id+"F0.wireOp",EDGE,"E72"),sQuery(id+"F0.wireOp",EDGE,"E73"),sQuery(id+"F0.wireOp",EDGE,"E74"),sQuery(id+"F0.wireOp",EDGE,"E75"),sQuery(id+"F0.wireOp",EDGE,"E76"),sQuery(id+"F0.wireOp",EDGE,"E77"),sQuery(id+"F0.wireOp",EDGE,"E78"),sQuery(id+"F0.wireOp",EDGE,"E79"),sQuery(id+"F0.wireOp",EDGE,"E80"),sQuery(id+"F0.wireOp",EDGE,"E81"),sQuery(id+"F0.wireOp",EDGE,"E82"),sQuery(id+"F0.wireOp",EDGE,"E83"),sQuery(id+"F0.wireOp",EDGE,"E84"),sQuery(id+"F0.wireOp",EDGE,"E85"),sQuery(id+"F0.wireOp",EDGE,"E86"),sQuery(id+"F0.wireOp",EDGE,"E87"),sQuery(id+"F0.wireOp",EDGE,"E88"),sQuery(id+"F0.wireOp",EDGE,"E89"),sQuery(id+"F0.wireOp",EDGE,"E90"),sQuery(id+"F0.wireOp",EDGE,"E91"),sQuery(id+"F0.wireOp",EDGE,"E92"),sQuery(id+"F0.wireOp",EDGE,"E93"),sQuery(id+"F0.wireOp",EDGE,"E94"),sQuery(id+"F0.wireOp",EDGE,"E95"),sQuery(id+"F0.wireOp",EDGE,"E96"),sQuery(id+"F0.wireOp",EDGE,"E97"),sQuery(id+"F0.wireOp",EDGE,"E98"),sQuery(id+"F0.wireOp",EDGE,"E99"),sQuery(id+"F0.wireOp",EDGE,"E100"),sQuery(id+"F0.wireOp",EDGE,"E101"),sQuery(id+"F0.wireOp",EDGE,"E102"),sQuery(id+"F0.wireOp",EDGE,"E103"),sQuery(id+"F0.wireOp",EDGE,"E104"),sQuery(id+"F0.wireOp",EDGE,"E105"),sQuery(id+"F0.wireOp",EDGE,"E106"),sQuery(id+"F0.wireOp",EDGE,"E107"),sQuery(id+"F0.wireOp",EDGE,"E108"),sQuery(id+"F0.wireOp",EDGE,"E109"),sQuery(id+"F0.wireOp",EDGE,"E110"),sQuery(id+"F0.wireOp",EDGE,"E111"),sQuery(id+"F0.wireOp",EDGE,"E112"),sQuery(id+"F0.wireOp",EDGE,"E113"),sQuery(id+"F0.wireOp",EDGE,"E114"),sQuery(id+"F0.wireOp",EDGE,"E115"),sQuery(id+"F0.wireOp",EDGE,"E116"),sQuery(id+"F0.wireOp",EDGE,"E117"),sQuery(id+"F0.wireOp",EDGE,"E118"),sQuery(id+"F0.wireOp",EDGE,"E119"),sQuery(id+"F0.wireOp",EDGE,"E120"),sQuery(id+"F0.wireOp",EDGE,"E121"),sQuery(id+"F0.wireOp",EDGE,"E122"),sQuery(id+"F0.wireOp",EDGE,"E123"),sQuery(id+"F0.wireOp",EDGE,"E124"),sQuery(id+"F0.wireOp",EDGE,"E125"),sQuery(id+"F0.wireOp",EDGE,"E126"),sQuery(id+"F0.wireOp",EDGE,"E127"),sQuery(id+"F0.wireOp",EDGE,"E128"),sQuery(id+"F0.wireOp",EDGE,"E129"),sQuery(id+"F0.wireOp",EDGE,"E130"),sQuery(id+"F0.wireOp",EDGE,"E131"),sQuery(id+"F0.wireOp",EDGE,"E132"),sQuery(id+"F0.wireOp",EDGE,"E133"),sQuery(id+"F0.wireOp",EDGE,"E134"),sQuery(id+"F0.wireOp",EDGE,"E135"),sQuery(id+"F0.wireOp",EDGE,"E136"),sQuery(id+"F0.wireOp",EDGE,"E137"),sQuery(id+"F0.wireOp",EDGE,"E138"),sQuery(id+"F0.wireOp",EDGE,"E139"),sQuery(id+"F0.wireOp",EDGE,"E140"),sQuery(id+"F0.wireOp",EDGE,"E141"),sQuery(id+"F0.wireOp",EDGE,"E142"),sQuery(id+"F0.wireOp",EDGE,"E143"),sQuery(id+"F0.wireOp",EDGE,"E144"),sQuery(id+"F0.wireOp",EDGE,"E145"),sQuery(id+"F0.wireOp",EDGE,"E146"),sQuery(id+"F0.wireOp",EDGE,"E147"),sQuery(id+"F0.wireOp",EDGE,"E148"),sQuery(id+"F0.wireOp",EDGE,"E149"),sQuery(id+"F0.wireOp",EDGE,"E150"),sQuery(id+"F0.wireOp",EDGE,"E151"),sQuery(id+"F0.wireOp",EDGE,"E152"),sQuery(id+"F0.wireOp",EDGE,"E153"),sQuery(id+"F0.wireOp",EDGE,"E154"),sQuery(id+"F0.wireOp",EDGE,"E155"),sQuery(id+"F0.wireOp",EDGE,"E156"),sQuery(id+"F0.wireOp",EDGE,"E157"),sQuery(id+"F0.wireOp",EDGE,"E158"),sQuery(id+"F0.wireOp",EDGE,"E159"),sQuery(id+"F0.wireOp",EDGE,"E160"),sQuery(id+"F0.wireOp",EDGE,"E161"),sQuery(id+"F0.wireOp",EDGE,"E162"),sQuery(id+"F0.wireOp",EDGE,"E163"),sQuery(id+"F0.wireOp",EDGE,"E164"),sQuery(id+"F0.wireOp",EDGE,"E165"),sQuery(id+"F0.wireOp",EDGE,"E166"),sQuery(id+"F0.wireOp",EDGE,"E167"),sQuery(id+"F0.wireOp",EDGE,"E168"),sQuery(id+"F0.wireOp",EDGE,"E169"),sQuery(id+"F0.wireOp",EDGE,"E170"),sQuery(id+"F0.wireOp",EDGE,"E171"),sQuery(id+"F0.wireOp",EDGE,"E172"),sQuery(id+"F0.wireOp",EDGE,"E173"),sQuery(id+"F0.wireOp",EDGE,"E174"),sQuery(id+"F0.wireOp",EDGE,"E175"),sQuery(id+"F0.wireOp",EDGE,"E176"),sQuery(id+"F0.wireOp",EDGE,"E177"),sQuery(id+"F0.wireOp",EDGE,"E178"),sQuery(id+"F0.wireOp",EDGE,"E179"),sQuery(id+"F0.wireOp",EDGE,"E180"),sQuery(id+"F0.wireOp",EDGE,"E181"),sQuery(id+"F0.wireOp",EDGE,"E182"),sQuery(id+"F0.wireOp",EDGE,"E183"),sQuery(id+"F0.wireOp",EDGE,"E184"),sQuery(id+"F0.wireOp",EDGE,"E185"),sQuery(id+"F0.wireOp",EDGE,"E186"),sQuery(id+"F0.wireOp",EDGE,"E187"),sQuery(id+"F0.wireOp",EDGE,"E188"),sQuery(id+"F0.wireOp",EDGE,"E189"),sQuery(id+"F0.wireOp",EDGE,"E190"),sQuery(id+"F0.wireOp",EDGE,"E191"),sQuery(id+"F0.wireOp",EDGE,"E192"),sQuery(id+"F0.wireOp",EDGE,"E193"),sQuery(id+"F0.wireOp",EDGE,"E194"),sQuery(id+"F0.wireOp",EDGE,"E195"),sQuery(id+"F0.wireOp",EDGE,"E196"),sQuery(id+"F0.wireOp",EDGE,"E197"),sQuery(id+"F0.wireOp",EDGE,"E198"),sQuery(id+"F0.wireOp",EDGE,"E199"),sQuery(id+"F0.wireOp",EDGE,"E200"),sQuery(id+"F0.wireOp",EDGE,"E201"),sQuery(id+"F0.wireOp",EDGE,"E202"),sQuery(id+"F0.wireOp",EDGE,"E203"),sQuery(id+"F0.wireOp",EDGE,"E204"),sQuery(id+"F0.wireOp",EDGE,"E205"),sQuery(id+"F0.wireOp",EDGE,"E206"),sQuery(id+"F0.wireOp",EDGE,"E207"),sQuery(id+"F0.wireOp",EDGE,"E208"),sQuery(id+"F0.wireOp",EDGE,"E209"),sQuery(id+"F0.wireOp",EDGE,"E210"),sQuery(id+"F0.wireOp",EDGE,"E211"),sQuery(id+"F0.wireOp",EDGE,"E212"),sQuery(id+"F0.wireOp",EDGE,"E213"),sQuery(id+"F0.wireOp",EDGE,"E214"),sQuery(id+"F0.wireOp",EDGE,"E215"),sQuery(id+"F0.wireOp",EDGE,"E216"),sQuery(id+"F0.wireOp",EDGE,"E217"),sQuery(id+"F0.wireOp",EDGE,"E218"),sQuery(id+"F0.wireOp",EDGE,"E219"),sQuery(id+"F0.wireOp",EDGE,"E220"),sQuery(id+"F0.wireOp",EDGE,"E221"),sQuery(id+"F0.wireOp",EDGE,"E222"),sQuery(id+"F0.wireOp",EDGE,"E223"),sQuery(id+"F0.wireOp",EDGE,"E224"),sQuery(id+"F0.wireOp",EDGE,"E225")])]});
            transform(context, id + "F3", {"entities" : qUnion([Q0]), "transformType" : TransformType.TRANSLATION_3D, "dx" : 127.23 * mm, "dy" : 0 * mm, "dz" : 23.1 * mm, "makeCopy" : false});
        }
        {
            var Q0;
            Q0=qCreatedBy(makeId("Front.planeOp"),FACE);
            var sketch = newSketch(context, id + "F4", { "sketchPlane" : qUnion([Q0])});
            skLineSegment(sketch, "E226", {"start": v(-132.34, 29.13) * mm, "end": v(-132.34, -22.68) * mm});
            skLineSegment(sketch, "E227", {"start": v(-132.34, -22.68) * mm, "end": v(-102.1, -22.88) * mm});
            skLineSegment(sketch, "E228", {"start": v(-102.1, -22.88) * mm, "end": v(-102.1, -18.85) * mm});
            skLineSegment(sketch, "E229", {"start": v(-102.1, -18.85) * mm, "end": v(-125.69, -19.05) * mm});
            skLineSegment(sketch, "E230", {"start": v(-125.69, -19.05) * mm, "end": v(-124.88, 28.93) * mm});
            skLineSegment(sketch, "E231", {"start": v(-124.88, 28.93) * mm, "end": v(-132.34, 29.13) * mm});
            skLineSegment(sketch, "E232", {"start": v(-118.43, -12.6) * mm, "end": v(-118.23, 28.73) * mm});
            skLineSegment(sketch, "E233", {"start": v(-118.23, 28.73) * mm, "end": v(-102.91, 29.13) * mm});
            skLineSegment(sketch, "E234", {"start": v(-102.91, 29.13) * mm, "end": v(-102.5, 24.7) * mm});
            skLineSegment(sketch, "E235", {"start": v(-102.5, 24.7) * mm, "end": v(-111.58, 24.5) * mm});
            skLineSegment(sketch, "E236", {"start": v(-111.58, 24.5) * mm, "end": v(-111.58, 21.67) * mm});
            skLineSegment(sketch, "E237", {"start": v(-111.58, 21.67) * mm, "end": v(-98.07, 21.87) * mm});
            skLineSegment(sketch, "E238", {"start": v(-98.07, 21.87) * mm, "end": v(-98.07, 17.64) * mm});
            skLineSegment(sketch, "E239", {"start": v(-98.07, 17.64) * mm, "end": v(-111.78, 17.44) * mm});
            skLineSegment(sketch, "E240", {"start": v(-111.78, 17.44) * mm, "end": v(-111.18, -8.37) * mm});
            skLineSegment(sketch, "E241", {"start": v(-111.18, -8.37) * mm, "end": v(-101.7, -8.77) * mm});
            skLineSegment(sketch, "E242", {"start": v(-101.7, -8.77) * mm, "end": v(-101.5, -13.8) * mm});
            skLineSegment(sketch, "E243", {"start": v(-101.5, -13.8) * mm, "end": v(-118.43, -12.6) * mm});
            skLineSegment(sketch, "E244", {"start": v(-95.65, -22.48) * mm, "end": v(-86.78, -22.48) * mm});
            skLineSegment(sketch, "E245", {"start": v(-86.78, -22.48) * mm, "end": v(-81.34, -18.65) * mm});
            skLineSegment(sketch, "E246", {"start": v(-81.34, -18.65) * mm, "end": v(-76.7, -11.39) * mm});
            skLineSegment(sketch, "E247", {"start": v(-76.7, -11.39) * mm, "end": v(-72.47, -3.12) * mm});
            skLineSegment(sketch, "E248", {"start": v(-72.47, -3.12) * mm, "end": v(-68.84, 4.13) * mm});
            skLineSegment(sketch, "E249", {"start": v(-68.84, 4.13) * mm, "end": v(-64.4, 13.2) * mm});
            skLineSegment(sketch, "E250", {"start": v(-64.4, 13.2) * mm, "end": v(-63.4, 17.44) * mm});
            skLineSegment(sketch, "E251", {"start": v(-63.4, 17.44) * mm, "end": v(-63.2, 23.28) * mm});
            skLineSegment(sketch, "E252", {"start": v(-63.2, 23.28) * mm, "end": v(-67.43, 26.91) * mm});
            skLineSegment(sketch, "E253", {"start": v(-67.43, 26.91) * mm, "end": v(-70.25, 28.12) * mm});
            skLineSegment(sketch, "E254", {"start": v(-70.25, 28.12) * mm, "end": v(-76.5, 28.93) * mm});
            skLineSegment(sketch, "E255", {"start": v(-76.5, 28.93) * mm, "end": v(-81.54, 28.73) * mm});
            skLineSegment(sketch, "E256", {"start": v(-81.54, 28.73) * mm, "end": v(-96.66, 28.93) * mm});
            skLineSegment(sketch, "E257", {"start": v(-96.66, 28.93) * mm, "end": v(-95.65, -22.48) * mm});
            skLineSegment(sketch, "E258", {"start": v(-68.24, -2.12) * mm, "end": v(-65.21, 3.53) * mm});
            skLineSegment(sketch, "E259", {"start": v(-65.21, 3.53) * mm, "end": v(-54.93, 3.53) * mm});
            skLineSegment(sketch, "E260", {"start": v(-54.93, 3.53) * mm, "end": v(-58.16, -3.12) * mm});
            skLineSegment(sketch, "E261", {"start": v(-58.16, -3.12) * mm, "end": v(-68.24, -2.12) * mm});
            skLineSegment(sketch, "E262", {"start": v(-65.82, -22.88) * mm, "end": v(-40.22, 24.5) * mm});
            skLineSegment(sketch, "E263", {"start": v(-40.22, 24.5) * mm, "end": v(-55.74, 23.89) * mm});
            skLineSegment(sketch, "E264", {"start": v(-55.74, 23.89) * mm, "end": v(-55.54, 28.73) * mm});
            skLineSegment(sketch, "E265", {"start": v(-55.54, 28.73) * mm, "end": v(-29.33, 28.93) * mm});
            skLineSegment(sketch, "E266", {"start": v(-29.33, 28.93) * mm, "end": v(-55.54, -18.65) * mm});
            skLineSegment(sketch, "E267", {"start": v(-55.54, -18.65) * mm, "end": v(-10.38, -18.24) * mm});
            skLineSegment(sketch, "E268", {"start": v(-10.38, -18.24) * mm, "end": v(-10.78, -23.69) * mm});
            skLineSegment(sketch, "E269", {"start": v(-10.78, -23.69) * mm, "end": v(-65.82, -22.88) * mm});
            skLineSegment(sketch, "E270", {"start": v(-27.52, -13.2) * mm, "end": v(-10.38, -13.2) * mm});
            skLineSegment(sketch, "E271", {"start": v(-10.38, -13.2) * mm, "end": v(-10.58, -8.77) * mm});
            skLineSegment(sketch, "E272", {"start": v(-10.58, -8.77) * mm, "end": v(-20.66, -8.77) * mm});
            skLineSegment(sketch, "E273", {"start": v(-20.66, -8.77) * mm, "end": v(-20.46, 18.04) * mm});
            skLineSegment(sketch, "E274", {"start": v(-20.46, 18.04) * mm, "end": v(-7.16, 17.44) * mm});
            skLineSegment(sketch, "E275", {"start": v(-7.16, 17.44) * mm, "end": v(-6.95, 21.67) * mm});
            skLineSegment(sketch, "E276", {"start": v(-6.95, 21.67) * mm, "end": v(-20.86, 21.67) * mm});
            skLineSegment(sketch, "E277", {"start": v(-20.86, 21.67) * mm, "end": v(-20.46, 24.9) * mm});
            skLineSegment(sketch, "E278", {"start": v(-20.46, 24.9) * mm, "end": v(-11.8, 24.9) * mm});
            skLineSegment(sketch, "E279", {"start": v(-11.8, 24.9) * mm, "end": v(-12.2, 28.93) * mm});
            skLineSegment(sketch, "E280", {"start": v(-12.2, 28.93) * mm, "end": v(-27.52, 28.93) * mm});
            skLineSegment(sketch, "E281", {"start": v(-27.52, 28.93) * mm, "end": v(-27.52, -13.2) * mm});
            skLineSegment(sketch, "E282", {"start": v(-4.94, -22.88) * mm, "end": v(2.32, -23.08) * mm});
            skLineSegment(sketch, "E283", {"start": v(2.32, -23.08) * mm, "end": v(1.92, 17.64) * mm});
            skLineSegment(sketch, "E284", {"start": v(1.92, 17.64) * mm, "end": v(17.24, 17.44) * mm});
            skLineSegment(sketch, "E285", {"start": v(17.24, 17.44) * mm, "end": v(21.07, 19.86) * mm});
            skLineSegment(sketch, "E286", {"start": v(21.07, 19.86) * mm, "end": v(21.67, 24.7) * mm});
            skLineSegment(sketch, "E287", {"start": v(21.67, 24.7) * mm, "end": v(16.23, 28.73) * mm});
            skLineSegment(sketch, "E288", {"start": v(16.23, 28.73) * mm, "end": v(-4.94, 28.73) * mm});
            skLineSegment(sketch, "E289", {"start": v(-4.94, 28.73) * mm, "end": v(-4.94, -22.88) * mm});
            skLineSegment(sketch, "E290", {"start": v(24.9, -22.48) * mm, "end": v(32.76, -23.08) * mm});
            skLineSegment(sketch, "E291", {"start": v(32.76, -23.08) * mm, "end": v(31.95, 17.64) * mm});
            skLineSegment(sketch, "E292", {"start": v(31.95, 17.64) * mm, "end": v(46.67, 17.64) * mm});
            skLineSegment(sketch, "E293", {"start": v(46.67, 17.64) * mm, "end": v(51.5, 20.66) * mm});
            skLineSegment(sketch, "E294", {"start": v(51.5, 20.66) * mm, "end": v(51.5, 26.1) * mm});
            skLineSegment(sketch, "E295", {"start": v(51.5, 26.1) * mm, "end": v(46.26, 28.93) * mm});
            skLineSegment(sketch, "E296", {"start": v(46.26, 28.93) * mm, "end": v(25.5, 28.93) * mm});
            skLineSegment(sketch, "E297", {"start": v(25.5, 28.93) * mm, "end": v(24.9, -22.48) * mm});
            skLineSegment(sketch, "E298", {"start": v(54.33, -23.48) * mm, "end": v(75.7, -23.89) * mm});
            skLineSegment(sketch, "E299", {"start": v(75.7, -23.89) * mm, "end": v(75.9, -19.25) * mm});
            skLineSegment(sketch, "E300", {"start": v(75.9, -19.25) * mm, "end": v(60.58, -18.85) * mm});
            skLineSegment(sketch, "E301", {"start": v(60.58, -18.85) * mm, "end": v(60.78, 17.64) * mm});
            skLineSegment(sketch, "E302", {"start": v(60.78, 17.64) * mm, "end": v(76.1, 17.44) * mm});
            skLineSegment(sketch, "E303", {"start": v(76.1, 17.44) * mm, "end": v(76.5, 20.86) * mm});
            skLineSegment(sketch, "E304", {"start": v(76.5, 20.86) * mm, "end": v(59.97, 21.07) * mm});
            skLineSegment(sketch, "E305", {"start": v(59.97, 21.07) * mm, "end": v(59.97, 24.09) * mm});
            skLineSegment(sketch, "E306", {"start": v(59.97, 24.09) * mm, "end": v(70.86, 24.3) * mm});
            skLineSegment(sketch, "E307", {"start": v(70.86, 24.3) * mm, "end": v(71.26, 28.32) * mm});
            skLineSegment(sketch, "E308", {"start": v(71.26, 28.32) * mm, "end": v(53.72, 28.52) * mm});
            skLineSegment(sketch, "E309", {"start": v(53.72, 28.52) * mm, "end": v(54.33, -23.48) * mm});
            skLineSegment(sketch, "E310", {"start": v(78.92, -23.69) * mm, "end": v(103.11, -23.89) * mm});
            skLineSegment(sketch, "E311", {"start": v(103.11, -23.89) * mm, "end": v(103.31, -18.85) * mm});
            skLineSegment(sketch, "E312", {"start": v(103.31, -18.85) * mm, "end": v(85.37, -18.65) * mm});
            skLineSegment(sketch, "E313", {"start": v(85.37, -18.65) * mm, "end": v(86.18, 28.52) * mm});
            skLineSegment(sketch, "E314", {"start": v(86.18, 28.52) * mm, "end": v(79.12, 28.93) * mm});
            skLineSegment(sketch, "E315", {"start": v(79.12, 28.93) * mm, "end": v(78.92, -23.69) * mm});
            skLineSegment(sketch, "E316", {"start": v(93.23, -12.6) * mm, "end": v(99.89, -12.8) * mm});
            skLineSegment(sketch, "E317", {"start": v(99.89, -12.8) * mm, "end": v(100.7, 28.32) * mm});
            skLineSegment(sketch, "E318", {"start": v(100.7, 28.32) * mm, "end": v(93.03, 28.12) * mm});
            skLineSegment(sketch, "E319", {"start": v(93.03, 28.12) * mm, "end": v(93.23, -12.6) * mm});
            skLineSegment(sketch, "E320", {"start": v(108.55, -23.28) * mm, "end": v(116.01, -23.28) * mm});
            skLineSegment(sketch, "E321", {"start": v(116.01, -23.28) * mm, "end": v(115.4, 8.77) * mm});
            skLineSegment(sketch, "E322", {"start": v(115.4, 8.77) * mm, "end": v(124.28, -10.58) * mm});
            skLineSegment(sketch, "E323", {"start": v(124.28, -10.58) * mm, "end": v(124.68, -29.13) * mm});
            skLineSegment(sketch, "E324", {"start": v(124.68, -29.13) * mm, "end": v(132.34, -28.93) * mm});
            skLineSegment(sketch, "E325", {"start": v(132.34, -28.93) * mm, "end": v(132.34, 27.72) * mm});
            skLineSegment(sketch, "E326", {"start": v(132.34, 27.72) * mm, "end": v(124.48, 27.72) * mm});
            skLineSegment(sketch, "E327", {"start": v(124.48, 27.72) * mm, "end": v(124.68, 4.33) * mm});
            skLineSegment(sketch, "E328", {"start": v(124.68, 4.33) * mm, "end": v(115, 23.08) * mm});
            skLineSegment(sketch, "E329", {"start": v(115, 23.08) * mm, "end": v(115, 27.72) * mm});
            skLineSegment(sketch, "E330", {"start": v(115, 27.72) * mm, "end": v(107.95, 27.92) * mm});
            skLineSegment(sketch, "E331", {"start": v(107.95, 27.92) * mm, "end": v(108.55, -23.28) * mm});
            skSolve(sketch);
        }
        {
            var Q0;
            Q0=qSketchRegion(id+"F4",true);
            extrude(context, id + "F5", {"entities" : qUnion([Q0]), "depth" : 25.4 * mm});
        }
        {
            var Q0;
            Q0=makeQuery(id+"F5.opExtrude","SWEPT_BODY",BODY,{"disambiguationData":[OSD([sQuery(id+"F4.wireOp",EDGE,"E226"),sQuery(id+"F4.wireOp",EDGE,"E227"),sQuery(id+"F4.wireOp",EDGE,"E228"),sQuery(id+"F4.wireOp",EDGE,"E229"),sQuery(id+"F4.wireOp",EDGE,"E230"),sQuery(id+"F4.wireOp",EDGE,"E231")])]});
            var Q1;
            Q1=makeQuery(id+"F5.opExtrude","SWEPT_BODY",BODY,{"disambiguationData":[OSD([sQuery(id+"F4.wireOp",EDGE,"E232"),sQuery(id+"F4.wireOp",EDGE,"E233"),sQuery(id+"F4.wireOp",EDGE,"E234"),sQuery(id+"F4.wireOp",EDGE,"E235"),sQuery(id+"F4.wireOp",EDGE,"E236"),sQuery(id+"F4.wireOp",EDGE,"E237"),sQuery(id+"F4.wireOp",EDGE,"E238"),sQuery(id+"F4.wireOp",EDGE,"E239"),sQuery(id+"F4.wireOp",EDGE,"E240"),sQuery(id+"F4.wireOp",EDGE,"E241"),sQuery(id+"F4.wireOp",EDGE,"E242"),sQuery(id+"F4.wireOp",EDGE,"E243")])]});
            var Q2;
            Q2=makeQuery(id+"F5.opExtrude","SWEPT_BODY",BODY,{"disambiguationData":[OSD([sQuery(id+"F4.wireOp",EDGE,"E244"),sQuery(id+"F4.wireOp",EDGE,"E245"),sQuery(id+"F4.wireOp",EDGE,"E246"),sQuery(id+"F4.wireOp",EDGE,"E247"),sQuery(id+"F4.wireOp",EDGE,"E248"),sQuery(id+"F4.wireOp",EDGE,"E249"),sQuery(id+"F4.wireOp",EDGE,"E250"),sQuery(id+"F4.wireOp",EDGE,"E251"),sQuery(id+"F4.wireOp",EDGE,"E252"),sQuery(id+"F4.wireOp",EDGE,"E253"),sQuery(id+"F4.wireOp",EDGE,"E254"),sQuery(id+"F4.wireOp",EDGE,"E255"),sQuery(id+"F4.wireOp",EDGE,"E256"),sQuery(id+"F4.wireOp",EDGE,"E257")])]});
            var Q3;
            Q3=makeQuery(id+"F5.opExtrude","SWEPT_BODY",BODY,{"disambiguationData":[OSD([sQuery(id+"F4.wireOp",EDGE,"E258"),sQuery(id+"F4.wireOp",EDGE,"E259"),sQuery(id+"F4.wireOp",EDGE,"E260"),sQuery(id+"F4.wireOp",EDGE,"E261")])]});
            var Q4;
            Q4=makeQuery(id+"F5.opExtrude","SWEPT_BODY",BODY,{"disambiguationData":[OSD([sQuery(id+"F4.wireOp",EDGE,"E262"),sQuery(id+"F4.wireOp",EDGE,"E263"),sQuery(id+"F4.wireOp",EDGE,"E264"),sQuery(id+"F4.wireOp",EDGE,"E265"),sQuery(id+"F4.wireOp",EDGE,"E266"),sQuery(id+"F4.wireOp",EDGE,"E267"),sQuery(id+"F4.wireOp",EDGE,"E268"),sQuery(id+"F4.wireOp",EDGE,"E269")])]});
            var Q5;
            Q5=makeQuery(id+"F5.opExtrude","SWEPT_BODY",BODY,{"disambiguationData":[OSD([sQuery(id+"F4.wireOp",EDGE,"E270"),sQuery(id+"F4.wireOp",EDGE,"E271"),sQuery(id+"F4.wireOp",EDGE,"E272"),sQuery(id+"F4.wireOp",EDGE,"E273"),sQuery(id+"F4.wireOp",EDGE,"E274"),sQuery(id+"F4.wireOp",EDGE,"E275"),sQuery(id+"F4.wireOp",EDGE,"E276"),sQuery(id+"F4.wireOp",EDGE,"E277"),sQuery(id+"F4.wireOp",EDGE,"E278"),sQuery(id+"F4.wireOp",EDGE,"E279"),sQuery(id+"F4.wireOp",EDGE,"E280"),sQuery(id+"F4.wireOp",EDGE,"E281")])]});
            var Q6;
            Q6=makeQuery(id+"F5.opExtrude","SWEPT_BODY",BODY,{"disambiguationData":[OSD([sQuery(id+"F4.wireOp",EDGE,"E282"),sQuery(id+"F4.wireOp",EDGE,"E283"),sQuery(id+"F4.wireOp",EDGE,"E284"),sQuery(id+"F4.wireOp",EDGE,"E285"),sQuery(id+"F4.wireOp",EDGE,"E286"),sQuery(id+"F4.wireOp",EDGE,"E287"),sQuery(id+"F4.wireOp",EDGE,"E288"),sQuery(id+"F4.wireOp",EDGE,"E289")])]});
            var Q7;
            Q7=makeQuery(id+"F5.opExtrude","SWEPT_BODY",BODY,{"disambiguationData":[OSD([sQuery(id+"F4.wireOp",EDGE,"E290"),sQuery(id+"F4.wireOp",EDGE,"E291"),sQuery(id+"F4.wireOp",EDGE,"E292"),sQuery(id+"F4.wireOp",EDGE,"E293"),sQuery(id+"F4.wireOp",EDGE,"E294"),sQuery(id+"F4.wireOp",EDGE,"E295"),sQuery(id+"F4.wireOp",EDGE,"E296"),sQuery(id+"F4.wireOp",EDGE,"E297")])]});
            var Q8;
            Q8=makeQuery(id+"F5.opExtrude","SWEPT_BODY",BODY,{"disambiguationData":[OSD([sQuery(id+"F4.wireOp",EDGE,"E298"),sQuery(id+"F4.wireOp",EDGE,"E299"),sQuery(id+"F4.wireOp",EDGE,"E300"),sQuery(id+"F4.wireOp",EDGE,"E301"),sQuery(id+"F4.wireOp",EDGE,"E302"),sQuery(id+"F4.wireOp",EDGE,"E303"),sQuery(id+"F4.wireOp",EDGE,"E304"),sQuery(id+"F4.wireOp",EDGE,"E305"),sQuery(id+"F4.wireOp",EDGE,"E306"),sQuery(id+"F4.wireOp",EDGE,"E307"),sQuery(id+"F4.wireOp",EDGE,"E308"),sQuery(id+"F4.wireOp",EDGE,"E309")])]});
            var Q9;
            Q9=makeQuery(id+"F5.opExtrude","SWEPT_BODY",BODY,{"disambiguationData":[OSD([sQuery(id+"F4.wireOp",EDGE,"E310"),sQuery(id+"F4.wireOp",EDGE,"E311"),sQuery(id+"F4.wireOp",EDGE,"E312"),sQuery(id+"F4.wireOp",EDGE,"E313"),sQuery(id+"F4.wireOp",EDGE,"E314"),sQuery(id+"F4.wireOp",EDGE,"E315")])]});
            var Q10;
            Q10=makeQuery(id+"F5.opExtrude","SWEPT_BODY",BODY,{"disambiguationData":[OSD([sQuery(id+"F4.wireOp",EDGE,"E316"),sQuery(id+"F4.wireOp",EDGE,"E317"),sQuery(id+"F4.wireOp",EDGE,"E318"),sQuery(id+"F4.wireOp",EDGE,"E319")])]});
            var Q11;
            Q11=makeQuery(id+"F5.opExtrude","SWEPT_BODY",BODY,{"disambiguationData":[OSD([sQuery(id+"F4.wireOp",EDGE,"E320"),sQuery(id+"F4.wireOp",EDGE,"E321"),sQuery(id+"F4.wireOp",EDGE,"E322"),sQuery(id+"F4.wireOp",EDGE,"E323"),sQuery(id+"F4.wireOp",EDGE,"E324"),sQuery(id+"F4.wireOp",EDGE,"E325"),sQuery(id+"F4.wireOp",EDGE,"E326"),sQuery(id+"F4.wireOp",EDGE,"E327"),sQuery(id+"F4.wireOp",EDGE,"E328"),sQuery(id+"F4.wireOp",EDGE,"E329"),sQuery(id+"F4.wireOp",EDGE,"E330"),sQuery(id+"F4.wireOp",EDGE,"E331")])]});
            var Q12;
            Q12=makeQuery(id+"F5.opExtrude","CAP_VERTEX",VERTEX,{"disambiguationData":[OSD([sQuery(id+"F4.wireOp",EDGE,"E325"),sQuery(id+"F4.wireOp",EDGE,"E326")])],"isStart":false});
            transform(context, id + "F6", {"entities" : qUnion([Q0, Q1, Q2, Q3, Q4, Q5, Q6, Q7, Q8, Q9, Q10, Q11]), "transformType" : TransformType.SCALE_UNIFORMLY, "scale" : .2, "makeCopy" : false, "scalePoint" : qUnion([Q12])});
        }
        {
            var Q0;
            Q0=makeQuery(id+"F1.opExtrude","SWEPT_BODY",BODY,{"disambiguationData":[OSD([sQuery(id+"F0.wireOp",EDGE,"E0"),sQuery(id+"F0.wireOp",EDGE,"E1"),sQuery(id+"F0.wireOp",EDGE,"E2"),sQuery(id+"F0.wireOp",EDGE,"E3"),sQuery(id+"F0.wireOp",EDGE,"E4"),sQuery(id+"F0.wireOp",EDGE,"E5"),sQuery(id+"F0.wireOp",EDGE,"E6"),sQuery(id+"F0.wireOp",EDGE,"E7"),sQuery(id+"F0.wireOp",EDGE,"E8"),sQuery(id+"F0.wireOp",EDGE,"E9"),sQuery(id+"F0.wireOp",EDGE,"E10"),sQuery(id+"F0.wireOp",EDGE,"E11"),sQuery(id+"F0.wireOp",EDGE,"E12"),sQuery(id+"F0.wireOp",EDGE,"E13"),sQuery(id+"F0.wireOp",EDGE,"E14"),sQuery(id+"F0.wireOp",EDGE,"E15"),sQuery(id+"F0.wireOp",EDGE,"E16"),sQuery(id+"F0.wireOp",EDGE,"E17"),sQuery(id+"F0.wireOp",EDGE,"E18"),sQuery(id+"F0.wireOp",EDGE,"E19"),sQuery(id+"F0.wireOp",EDGE,"E20"),sQuery(id+"F0.wireOp",EDGE,"E21"),sQuery(id+"F0.wireOp",EDGE,"E22"),sQuery(id+"F0.wireOp",EDGE,"E23"),sQuery(id+"F0.wireOp",EDGE,"E24"),sQuery(id+"F0.wireOp",EDGE,"E25"),sQuery(id+"F0.wireOp",EDGE,"E26"),sQuery(id+"F0.wireOp",EDGE,"E27"),sQuery(id+"F0.wireOp",EDGE,"E28"),sQuery(id+"F0.wireOp",EDGE,"E29"),sQuery(id+"F0.wireOp",EDGE,"E30"),sQuery(id+"F0.wireOp",EDGE,"E31"),sQuery(id+"F0.wireOp",EDGE,"E32"),sQuery(id+"F0.wireOp",EDGE,"E33"),sQuery(id+"F0.wireOp",EDGE,"E34"),sQuery(id+"F0.wireOp",EDGE,"E35"),sQuery(id+"F0.wireOp",EDGE,"E36"),sQuery(id+"F0.wireOp",EDGE,"E37"),sQuery(id+"F0.wireOp",EDGE,"E38"),sQuery(id+"F0.wireOp",EDGE,"E39"),sQuery(id+"F0.wireOp",EDGE,"E40"),sQuery(id+"F0.wireOp",EDGE,"E41"),sQuery(id+"F0.wireOp",EDGE,"E42"),sQuery(id+"F0.wireOp",EDGE,"E43"),sQuery(id+"F0.wireOp",EDGE,"E44"),sQuery(id+"F0.wireOp",EDGE,"E45"),sQuery(id+"F0.wireOp",EDGE,"E46"),sQuery(id+"F0.wireOp",EDGE,"E47"),sQuery(id+"F0.wireOp",EDGE,"E48"),sQuery(id+"F0.wireOp",EDGE,"E49"),sQuery(id+"F0.wireOp",EDGE,"E50"),sQuery(id+"F0.wireOp",EDGE,"E51"),sQuery(id+"F0.wireOp",EDGE,"E52"),sQuery(id+"F0.wireOp",EDGE,"E53"),sQuery(id+"F0.wireOp",EDGE,"E54"),sQuery(id+"F0.wireOp",EDGE,"E55"),sQuery(id+"F0.wireOp",EDGE,"E56"),sQuery(id+"F0.wireOp",EDGE,"E57"),sQuery(id+"F0.wireOp",EDGE,"E58"),sQuery(id+"F0.wireOp",EDGE,"E59"),sQuery(id+"F0.wireOp",EDGE,"E60"),sQuery(id+"F0.wireOp",EDGE,"E61"),sQuery(id+"F0.wireOp",EDGE,"E62"),sQuery(id+"F0.wireOp",EDGE,"E63"),sQuery(id+"F0.wireOp",EDGE,"E64"),sQuery(id+"F0.wireOp",EDGE,"E65"),sQuery(id+"F0.wireOp",EDGE,"E66"),sQuery(id+"F0.wireOp",EDGE,"E67"),sQuery(id+"F0.wireOp",EDGE,"E68"),sQuery(id+"F0.wireOp",EDGE,"E69"),sQuery(id+"F0.wireOp",EDGE,"E70"),sQuery(id+"F0.wireOp",EDGE,"E71"),sQuery(id+"F0.wireOp",EDGE,"E72"),sQuery(id+"F0.wireOp",EDGE,"E73"),sQuery(id+"F0.wireOp",EDGE,"E74"),sQuery(id+"F0.wireOp",EDGE,"E75"),sQuery(id+"F0.wireOp",EDGE,"E76"),sQuery(id+"F0.wireOp",EDGE,"E77"),sQuery(id+"F0.wireOp",EDGE,"E78"),sQuery(id+"F0.wireOp",EDGE,"E79"),sQuery(id+"F0.wireOp",EDGE,"E80"),sQuery(id+"F0.wireOp",EDGE,"E81"),sQuery(id+"F0.wireOp",EDGE,"E82"),sQuery(id+"F0.wireOp",EDGE,"E83"),sQuery(id+"F0.wireOp",EDGE,"E84"),sQuery(id+"F0.wireOp",EDGE,"E85"),sQuery(id+"F0.wireOp",EDGE,"E86"),sQuery(id+"F0.wireOp",EDGE,"E87"),sQuery(id+"F0.wireOp",EDGE,"E88"),sQuery(id+"F0.wireOp",EDGE,"E89"),sQuery(id+"F0.wireOp",EDGE,"E90"),sQuery(id+"F0.wireOp",EDGE,"E91"),sQuery(id+"F0.wireOp",EDGE,"E92"),sQuery(id+"F0.wireOp",EDGE,"E93"),sQuery(id+"F0.wireOp",EDGE,"E94"),sQuery(id+"F0.wireOp",EDGE,"E95"),sQuery(id+"F0.wireOp",EDGE,"E96"),sQuery(id+"F0.wireOp",EDGE,"E97"),sQuery(id+"F0.wireOp",EDGE,"E98"),sQuery(id+"F0.wireOp",EDGE,"E99"),sQuery(id+"F0.wireOp",EDGE,"E100"),sQuery(id+"F0.wireOp",EDGE,"E101"),sQuery(id+"F0.wireOp",EDGE,"E102"),sQuery(id+"F0.wireOp",EDGE,"E103"),sQuery(id+"F0.wireOp",EDGE,"E104"),sQuery(id+"F0.wireOp",EDGE,"E105"),sQuery(id+"F0.wireOp",EDGE,"E106"),sQuery(id+"F0.wireOp",EDGE,"E107"),sQuery(id+"F0.wireOp",EDGE,"E108"),sQuery(id+"F0.wireOp",EDGE,"E109"),sQuery(id+"F0.wireOp",EDGE,"E110"),sQuery(id+"F0.wireOp",EDGE,"E111"),sQuery(id+"F0.wireOp",EDGE,"E112"),sQuery(id+"F0.wireOp",EDGE,"E113"),sQuery(id+"F0.wireOp",EDGE,"E114"),sQuery(id+"F0.wireOp",EDGE,"E115"),sQuery(id+"F0.wireOp",EDGE,"E116"),sQuery(id+"F0.wireOp",EDGE,"E117"),sQuery(id+"F0.wireOp",EDGE,"E118"),sQuery(id+"F0.wireOp",EDGE,"E119"),sQuery(id+"F0.wireOp",EDGE,"E120"),sQuery(id+"F0.wireOp",EDGE,"E121"),sQuery(id+"F0.wireOp",EDGE,"E122"),sQuery(id+"F0.wireOp",EDGE,"E123"),sQuery(id+"F0.wireOp",EDGE,"E124"),sQuery(id+"F0.wireOp",EDGE,"E125"),sQuery(id+"F0.wireOp",EDGE,"E126"),sQuery(id+"F0.wireOp",EDGE,"E127"),sQuery(id+"F0.wireOp",EDGE,"E128"),sQuery(id+"F0.wireOp",EDGE,"E129"),sQuery(id+"F0.wireOp",EDGE,"E130"),sQuery(id+"F0.wireOp",EDGE,"E131"),sQuery(id+"F0.wireOp",EDGE,"E132"),sQuery(id+"F0.wireOp",EDGE,"E133"),sQuery(id+"F0.wireOp",EDGE,"E134"),sQuery(id+"F0.wireOp",EDGE,"E135"),sQuery(id+"F0.wireOp",EDGE,"E136"),sQuery(id+"F0.wireOp",EDGE,"E137"),sQuery(id+"F0.wireOp",EDGE,"E138"),sQuery(id+"F0.wireOp",EDGE,"E139"),sQuery(id+"F0.wireOp",EDGE,"E140"),sQuery(id+"F0.wireOp",EDGE,"E141"),sQuery(id+"F0.wireOp",EDGE,"E142"),sQuery(id+"F0.wireOp",EDGE,"E143"),sQuery(id+"F0.wireOp",EDGE,"E144"),sQuery(id+"F0.wireOp",EDGE,"E145"),sQuery(id+"F0.wireOp",EDGE,"E146"),sQuery(id+"F0.wireOp",EDGE,"E147"),sQuery(id+"F0.wireOp",EDGE,"E148"),sQuery(id+"F0.wireOp",EDGE,"E149"),sQuery(id+"F0.wireOp",EDGE,"E150"),sQuery(id+"F0.wireOp",EDGE,"E151"),sQuery(id+"F0.wireOp",EDGE,"E152"),sQuery(id+"F0.wireOp",EDGE,"E153"),sQuery(id+"F0.wireOp",EDGE,"E154"),sQuery(id+"F0.wireOp",EDGE,"E155"),sQuery(id+"F0.wireOp",EDGE,"E156"),sQuery(id+"F0.wireOp",EDGE,"E157"),sQuery(id+"F0.wireOp",EDGE,"E158"),sQuery(id+"F0.wireOp",EDGE,"E159"),sQuery(id+"F0.wireOp",EDGE,"E160"),sQuery(id+"F0.wireOp",EDGE,"E161"),sQuery(id+"F0.wireOp",EDGE,"E162"),sQuery(id+"F0.wireOp",EDGE,"E163"),sQuery(id+"F0.wireOp",EDGE,"E164"),sQuery(id+"F0.wireOp",EDGE,"E165"),sQuery(id+"F0.wireOp",EDGE,"E166"),sQuery(id+"F0.wireOp",EDGE,"E167"),sQuery(id+"F0.wireOp",EDGE,"E168"),sQuery(id+"F0.wireOp",EDGE,"E169"),sQuery(id+"F0.wireOp",EDGE,"E170"),sQuery(id+"F0.wireOp",EDGE,"E171"),sQuery(id+"F0.wireOp",EDGE,"E172"),sQuery(id+"F0.wireOp",EDGE,"E173"),sQuery(id+"F0.wireOp",EDGE,"E174"),sQuery(id+"F0.wireOp",EDGE,"E175"),sQuery(id+"F0.wireOp",EDGE,"E176"),sQuery(id+"F0.wireOp",EDGE,"E177"),sQuery(id+"F0.wireOp",EDGE,"E178"),sQuery(id+"F0.wireOp",EDGE,"E179"),sQuery(id+"F0.wireOp",EDGE,"E180"),sQuery(id+"F0.wireOp",EDGE,"E181"),sQuery(id+"F0.wireOp",EDGE,"E182"),sQuery(id+"F0.wireOp",EDGE,"E183"),sQuery(id+"F0.wireOp",EDGE,"E184"),sQuery(id+"F0.wireOp",EDGE,"E185"),sQuery(id+"F0.wireOp",EDGE,"E186"),sQuery(id+"F0.wireOp",EDGE,"E187"),sQuery(id+"F0.wireOp",EDGE,"E188"),sQuery(id+"F0.wireOp",EDGE,"E189"),sQuery(id+"F0.wireOp",EDGE,"E190"),sQuery(id+"F0.wireOp",EDGE,"E191"),sQuery(id+"F0.wireOp",EDGE,"E192"),sQuery(id+"F0.wireOp",EDGE,"E193"),sQuery(id+"F0.wireOp",EDGE,"E194"),sQuery(id+"F0.wireOp",EDGE,"E195"),sQuery(id+"F0.wireOp",EDGE,"E196"),sQuery(id+"F0.wireOp",EDGE,"E197"),sQuery(id+"F0.wireOp",EDGE,"E198"),sQuery(id+"F0.wireOp",EDGE,"E199"),sQuery(id+"F0.wireOp",EDGE,"E200"),sQuery(id+"F0.wireOp",EDGE,"E201"),sQuery(id+"F0.wireOp",EDGE,"E202"),sQuery(id+"F0.wireOp",EDGE,"E203"),sQuery(id+"F0.wireOp",EDGE,"E204"),sQuery(id+"F0.wireOp",EDGE,"E205"),sQuery(id+"F0.wireOp",EDGE,"E206"),sQuery(id+"F0.wireOp",EDGE,"E207"),sQuery(id+"F0.wireOp",EDGE,"E208"),sQuery(id+"F0.wireOp",EDGE,"E209"),sQuery(id+"F0.wireOp",EDGE,"E210"),sQuery(id+"F0.wireOp",EDGE,"E211"),sQuery(id+"F0.wireOp",EDGE,"E212"),sQuery(id+"F0.wireOp",EDGE,"E213"),sQuery(id+"F0.wireOp",EDGE,"E214"),sQuery(id+"F0.wireOp",EDGE,"E215"),sQuery(id+"F0.wireOp",EDGE,"E216"),sQuery(id+"F0.wireOp",EDGE,"E217"),sQuery(id+"F0.wireOp",EDGE,"E218"),sQuery(id+"F0.wireOp",EDGE,"E219"),sQuery(id+"F0.wireOp",EDGE,"E220"),sQuery(id+"F0.wireOp",EDGE,"E221"),sQuery(id+"F0.wireOp",EDGE,"E222"),sQuery(id+"F0.wireOp",EDGE,"E223"),sQuery(id+"F0.wireOp",EDGE,"E224"),sQuery(id+"F0.wireOp",EDGE,"E225")])]});
            transform(context, id + "F7", {"entities" : qUnion([Q0]), "transformType" : TransformType.TRANSLATION_3D, "dx" : -53.8 * mm, "dy" : 0 * mm, "dz" : -58.65 * mm, "makeCopy" : false});
        }
        {
            var Q0;
            Q0=makeQuery(id+"F1.opExtrude","SWEPT_BODY",BODY,{"disambiguationData":[OSD([sQuery(id+"F0.wireOp",EDGE,"E0"),sQuery(id+"F0.wireOp",EDGE,"E1"),sQuery(id+"F0.wireOp",EDGE,"E2"),sQuery(id+"F0.wireOp",EDGE,"E3"),sQuery(id+"F0.wireOp",EDGE,"E4"),sQuery(id+"F0.wireOp",EDGE,"E5"),sQuery(id+"F0.wireOp",EDGE,"E6"),sQuery(id+"F0.wireOp",EDGE,"E7"),sQuery(id+"F0.wireOp",EDGE,"E8"),sQuery(id+"F0.wireOp",EDGE,"E9"),sQuery(id+"F0.wireOp",EDGE,"E10"),sQuery(id+"F0.wireOp",EDGE,"E11"),sQuery(id+"F0.wireOp",EDGE,"E12"),sQuery(id+"F0.wireOp",EDGE,"E13"),sQuery(id+"F0.wireOp",EDGE,"E14"),sQuery(id+"F0.wireOp",EDGE,"E15"),sQuery(id+"F0.wireOp",EDGE,"E16"),sQuery(id+"F0.wireOp",EDGE,"E17"),sQuery(id+"F0.wireOp",EDGE,"E18"),sQuery(id+"F0.wireOp",EDGE,"E19"),sQuery(id+"F0.wireOp",EDGE,"E20"),sQuery(id+"F0.wireOp",EDGE,"E21"),sQuery(id+"F0.wireOp",EDGE,"E22"),sQuery(id+"F0.wireOp",EDGE,"E23"),sQuery(id+"F0.wireOp",EDGE,"E24"),sQuery(id+"F0.wireOp",EDGE,"E25"),sQuery(id+"F0.wireOp",EDGE,"E26"),sQuery(id+"F0.wireOp",EDGE,"E27"),sQuery(id+"F0.wireOp",EDGE,"E28"),sQuery(id+"F0.wireOp",EDGE,"E29"),sQuery(id+"F0.wireOp",EDGE,"E30"),sQuery(id+"F0.wireOp",EDGE,"E31"),sQuery(id+"F0.wireOp",EDGE,"E32"),sQuery(id+"F0.wireOp",EDGE,"E33"),sQuery(id+"F0.wireOp",EDGE,"E34"),sQuery(id+"F0.wireOp",EDGE,"E35"),sQuery(id+"F0.wireOp",EDGE,"E36"),sQuery(id+"F0.wireOp",EDGE,"E37"),sQuery(id+"F0.wireOp",EDGE,"E38"),sQuery(id+"F0.wireOp",EDGE,"E39"),sQuery(id+"F0.wireOp",EDGE,"E40"),sQuery(id+"F0.wireOp",EDGE,"E41"),sQuery(id+"F0.wireOp",EDGE,"E42"),sQuery(id+"F0.wireOp",EDGE,"E43"),sQuery(id+"F0.wireOp",EDGE,"E44"),sQuery(id+"F0.wireOp",EDGE,"E45"),sQuery(id+"F0.wireOp",EDGE,"E46"),sQuery(id+"F0.wireOp",EDGE,"E47"),sQuery(id+"F0.wireOp",EDGE,"E48"),sQuery(id+"F0.wireOp",EDGE,"E49"),sQuery(id+"F0.wireOp",EDGE,"E50"),sQuery(id+"F0.wireOp",EDGE,"E51"),sQuery(id+"F0.wireOp",EDGE,"E52"),sQuery(id+"F0.wireOp",EDGE,"E53"),sQuery(id+"F0.wireOp",EDGE,"E54"),sQuery(id+"F0.wireOp",EDGE,"E55"),sQuery(id+"F0.wireOp",EDGE,"E56"),sQuery(id+"F0.wireOp",EDGE,"E57"),sQuery(id+"F0.wireOp",EDGE,"E58"),sQuery(id+"F0.wireOp",EDGE,"E59"),sQuery(id+"F0.wireOp",EDGE,"E60"),sQuery(id+"F0.wireOp",EDGE,"E61"),sQuery(id+"F0.wireOp",EDGE,"E62"),sQuery(id+"F0.wireOp",EDGE,"E63"),sQuery(id+"F0.wireOp",EDGE,"E64"),sQuery(id+"F0.wireOp",EDGE,"E65"),sQuery(id+"F0.wireOp",EDGE,"E66"),sQuery(id+"F0.wireOp",EDGE,"E67"),sQuery(id+"F0.wireOp",EDGE,"E68"),sQuery(id+"F0.wireOp",EDGE,"E69"),sQuery(id+"F0.wireOp",EDGE,"E70"),sQuery(id+"F0.wireOp",EDGE,"E71"),sQuery(id+"F0.wireOp",EDGE,"E72"),sQuery(id+"F0.wireOp",EDGE,"E73"),sQuery(id+"F0.wireOp",EDGE,"E74"),sQuery(id+"F0.wireOp",EDGE,"E75"),sQuery(id+"F0.wireOp",EDGE,"E76"),sQuery(id+"F0.wireOp",EDGE,"E77"),sQuery(id+"F0.wireOp",EDGE,"E78"),sQuery(id+"F0.wireOp",EDGE,"E79"),sQuery(id+"F0.wireOp",EDGE,"E80"),sQuery(id+"F0.wireOp",EDGE,"E81"),sQuery(id+"F0.wireOp",EDGE,"E82"),sQuery(id+"F0.wireOp",EDGE,"E83"),sQuery(id+"F0.wireOp",EDGE,"E84"),sQuery(id+"F0.wireOp",EDGE,"E85"),sQuery(id+"F0.wireOp",EDGE,"E86"),sQuery(id+"F0.wireOp",EDGE,"E87"),sQuery(id+"F0.wireOp",EDGE,"E88"),sQuery(id+"F0.wireOp",EDGE,"E89"),sQuery(id+"F0.wireOp",EDGE,"E90"),sQuery(id+"F0.wireOp",EDGE,"E91"),sQuery(id+"F0.wireOp",EDGE,"E92"),sQuery(id+"F0.wireOp",EDGE,"E93"),sQuery(id+"F0.wireOp",EDGE,"E94"),sQuery(id+"F0.wireOp",EDGE,"E95"),sQuery(id+"F0.wireOp",EDGE,"E96"),sQuery(id+"F0.wireOp",EDGE,"E97"),sQuery(id+"F0.wireOp",EDGE,"E98"),sQuery(id+"F0.wireOp",EDGE,"E99"),sQuery(id+"F0.wireOp",EDGE,"E100"),sQuery(id+"F0.wireOp",EDGE,"E101"),sQuery(id+"F0.wireOp",EDGE,"E102"),sQuery(id+"F0.wireOp",EDGE,"E103"),sQuery(id+"F0.wireOp",EDGE,"E104"),sQuery(id+"F0.wireOp",EDGE,"E105"),sQuery(id+"F0.wireOp",EDGE,"E106"),sQuery(id+"F0.wireOp",EDGE,"E107"),sQuery(id+"F0.wireOp",EDGE,"E108"),sQuery(id+"F0.wireOp",EDGE,"E109"),sQuery(id+"F0.wireOp",EDGE,"E110"),sQuery(id+"F0.wireOp",EDGE,"E111"),sQuery(id+"F0.wireOp",EDGE,"E112"),sQuery(id+"F0.wireOp",EDGE,"E113"),sQuery(id+"F0.wireOp",EDGE,"E114"),sQuery(id+"F0.wireOp",EDGE,"E115"),sQuery(id+"F0.wireOp",EDGE,"E116"),sQuery(id+"F0.wireOp",EDGE,"E117"),sQuery(id+"F0.wireOp",EDGE,"E118"),sQuery(id+"F0.wireOp",EDGE,"E119"),sQuery(id+"F0.wireOp",EDGE,"E120"),sQuery(id+"F0.wireOp",EDGE,"E121"),sQuery(id+"F0.wireOp",EDGE,"E122"),sQuery(id+"F0.wireOp",EDGE,"E123"),sQuery(id+"F0.wireOp",EDGE,"E124"),sQuery(id+"F0.wireOp",EDGE,"E125"),sQuery(id+"F0.wireOp",EDGE,"E126"),sQuery(id+"F0.wireOp",EDGE,"E127"),sQuery(id+"F0.wireOp",EDGE,"E128"),sQuery(id+"F0.wireOp",EDGE,"E129"),sQuery(id+"F0.wireOp",EDGE,"E130"),sQuery(id+"F0.wireOp",EDGE,"E131"),sQuery(id+"F0.wireOp",EDGE,"E132"),sQuery(id+"F0.wireOp",EDGE,"E133"),sQuery(id+"F0.wireOp",EDGE,"E134"),sQuery(id+"F0.wireOp",EDGE,"E135"),sQuery(id+"F0.wireOp",EDGE,"E136"),sQuery(id+"F0.wireOp",EDGE,"E137"),sQuery(id+"F0.wireOp",EDGE,"E138"),sQuery(id+"F0.wireOp",EDGE,"E139"),sQuery(id+"F0.wireOp",EDGE,"E140"),sQuery(id+"F0.wireOp",EDGE,"E141"),sQuery(id+"F0.wireOp",EDGE,"E142"),sQuery(id+"F0.wireOp",EDGE,"E143"),sQuery(id+"F0.wireOp",EDGE,"E144"),sQuery(id+"F0.wireOp",EDGE,"E145"),sQuery(id+"F0.wireOp",EDGE,"E146"),sQuery(id+"F0.wireOp",EDGE,"E147"),sQuery(id+"F0.wireOp",EDGE,"E148"),sQuery(id+"F0.wireOp",EDGE,"E149"),sQuery(id+"F0.wireOp",EDGE,"E150"),sQuery(id+"F0.wireOp",EDGE,"E151"),sQuery(id+"F0.wireOp",EDGE,"E152"),sQuery(id+"F0.wireOp",EDGE,"E153"),sQuery(id+"F0.wireOp",EDGE,"E154"),sQuery(id+"F0.wireOp",EDGE,"E155"),sQuery(id+"F0.wireOp",EDGE,"E156"),sQuery(id+"F0.wireOp",EDGE,"E157"),sQuery(id+"F0.wireOp",EDGE,"E158"),sQuery(id+"F0.wireOp",EDGE,"E159"),sQuery(id+"F0.wireOp",EDGE,"E160"),sQuery(id+"F0.wireOp",EDGE,"E161"),sQuery(id+"F0.wireOp",EDGE,"E162"),sQuery(id+"F0.wireOp",EDGE,"E163"),sQuery(id+"F0.wireOp",EDGE,"E164"),sQuery(id+"F0.wireOp",EDGE,"E165"),sQuery(id+"F0.wireOp",EDGE,"E166"),sQuery(id+"F0.wireOp",EDGE,"E167"),sQuery(id+"F0.wireOp",EDGE,"E168"),sQuery(id+"F0.wireOp",EDGE,"E169"),sQuery(id+"F0.wireOp",EDGE,"E170"),sQuery(id+"F0.wireOp",EDGE,"E171"),sQuery(id+"F0.wireOp",EDGE,"E172"),sQuery(id+"F0.wireOp",EDGE,"E173"),sQuery(id+"F0.wireOp",EDGE,"E174"),sQuery(id+"F0.wireOp",EDGE,"E175"),sQuery(id+"F0.wireOp",EDGE,"E176"),sQuery(id+"F0.wireOp",EDGE,"E177"),sQuery(id+"F0.wireOp",EDGE,"E178"),sQuery(id+"F0.wireOp",EDGE,"E179"),sQuery(id+"F0.wireOp",EDGE,"E180"),sQuery(id+"F0.wireOp",EDGE,"E181"),sQuery(id+"F0.wireOp",EDGE,"E182"),sQuery(id+"F0.wireOp",EDGE,"E183"),sQuery(id+"F0.wireOp",EDGE,"E184"),sQuery(id+"F0.wireOp",EDGE,"E185"),sQuery(id+"F0.wireOp",EDGE,"E186"),sQuery(id+"F0.wireOp",EDGE,"E187"),sQuery(id+"F0.wireOp",EDGE,"E188"),sQuery(id+"F0.wireOp",EDGE,"E189"),sQuery(id+"F0.wireOp",EDGE,"E190"),sQuery(id+"F0.wireOp",EDGE,"E191"),sQuery(id+"F0.wireOp",EDGE,"E192"),sQuery(id+"F0.wireOp",EDGE,"E193"),sQuery(id+"F0.wireOp",EDGE,"E194"),sQuery(id+"F0.wireOp",EDGE,"E195"),sQuery(id+"F0.wireOp",EDGE,"E196"),sQuery(id+"F0.wireOp",EDGE,"E197"),sQuery(id+"F0.wireOp",EDGE,"E198"),sQuery(id+"F0.wireOp",EDGE,"E199"),sQuery(id+"F0.wireOp",EDGE,"E200"),sQuery(id+"F0.wireOp",EDGE,"E201"),sQuery(id+"F0.wireOp",EDGE,"E202"),sQuery(id+"F0.wireOp",EDGE,"E203"),sQuery(id+"F0.wireOp",EDGE,"E204"),sQuery(id+"F0.wireOp",EDGE,"E205"),sQuery(id+"F0.wireOp",EDGE,"E206"),sQuery(id+"F0.wireOp",EDGE,"E207"),sQuery(id+"F0.wireOp",EDGE,"E208"),sQuery(id+"F0.wireOp",EDGE,"E209"),sQuery(id+"F0.wireOp",EDGE,"E210"),sQuery(id+"F0.wireOp",EDGE,"E211"),sQuery(id+"F0.wireOp",EDGE,"E212"),sQuery(id+"F0.wireOp",EDGE,"E213"),sQuery(id+"F0.wireOp",EDGE,"E214"),sQuery(id+"F0.wireOp",EDGE,"E215"),sQuery(id+"F0.wireOp",EDGE,"E216"),sQuery(id+"F0.wireOp",EDGE,"E217"),sQuery(id+"F0.wireOp",EDGE,"E218"),sQuery(id+"F0.wireOp",EDGE,"E219"),sQuery(id+"F0.wireOp",EDGE,"E220"),sQuery(id+"F0.wireOp",EDGE,"E221"),sQuery(id+"F0.wireOp",EDGE,"E222"),sQuery(id+"F0.wireOp",EDGE,"E223"),sQuery(id+"F0.wireOp",EDGE,"E224"),sQuery(id+"F0.wireOp",EDGE,"E225")])]});
            var Q1;
            Q1=makeQuery(id+"F1.opExtrude","CAP_VERTEX",VERTEX,{"disambiguationData":[OSD([sQuery(id+"F0.wireOp",EDGE,"E206"),sQuery(id+"F0.wireOp",EDGE,"E216")])],"isStart":false});
            transform(context, id + "F8", {"entities" : qUnion([Q0]), "transformType" : TransformType.SCALE_UNIFORMLY, "scale" : 4, "makeCopy" : false, "scalePoint" : qUnion([Q1])});
        }
        {
            var Q0;
            Q0=makeQuery(id+"F1.opExtrude","SWEPT_BODY",BODY,{"disambiguationData":[OSD([sQuery(id+"F0.wireOp",EDGE,"E0"),sQuery(id+"F0.wireOp",EDGE,"E1"),sQuery(id+"F0.wireOp",EDGE,"E2"),sQuery(id+"F0.wireOp",EDGE,"E3"),sQuery(id+"F0.wireOp",EDGE,"E4"),sQuery(id+"F0.wireOp",EDGE,"E5"),sQuery(id+"F0.wireOp",EDGE,"E6"),sQuery(id+"F0.wireOp",EDGE,"E7"),sQuery(id+"F0.wireOp",EDGE,"E8"),sQuery(id+"F0.wireOp",EDGE,"E9"),sQuery(id+"F0.wireOp",EDGE,"E10"),sQuery(id+"F0.wireOp",EDGE,"E11"),sQuery(id+"F0.wireOp",EDGE,"E12"),sQuery(id+"F0.wireOp",EDGE,"E13"),sQuery(id+"F0.wireOp",EDGE,"E14"),sQuery(id+"F0.wireOp",EDGE,"E15"),sQuery(id+"F0.wireOp",EDGE,"E16"),sQuery(id+"F0.wireOp",EDGE,"E17"),sQuery(id+"F0.wireOp",EDGE,"E18"),sQuery(id+"F0.wireOp",EDGE,"E19"),sQuery(id+"F0.wireOp",EDGE,"E20"),sQuery(id+"F0.wireOp",EDGE,"E21"),sQuery(id+"F0.wireOp",EDGE,"E22"),sQuery(id+"F0.wireOp",EDGE,"E23"),sQuery(id+"F0.wireOp",EDGE,"E24"),sQuery(id+"F0.wireOp",EDGE,"E25"),sQuery(id+"F0.wireOp",EDGE,"E26"),sQuery(id+"F0.wireOp",EDGE,"E27"),sQuery(id+"F0.wireOp",EDGE,"E28"),sQuery(id+"F0.wireOp",EDGE,"E29"),sQuery(id+"F0.wireOp",EDGE,"E30"),sQuery(id+"F0.wireOp",EDGE,"E31"),sQuery(id+"F0.wireOp",EDGE,"E32"),sQuery(id+"F0.wireOp",EDGE,"E33"),sQuery(id+"F0.wireOp",EDGE,"E34"),sQuery(id+"F0.wireOp",EDGE,"E35"),sQuery(id+"F0.wireOp",EDGE,"E36"),sQuery(id+"F0.wireOp",EDGE,"E37"),sQuery(id+"F0.wireOp",EDGE,"E38"),sQuery(id+"F0.wireOp",EDGE,"E39"),sQuery(id+"F0.wireOp",EDGE,"E40"),sQuery(id+"F0.wireOp",EDGE,"E41"),sQuery(id+"F0.wireOp",EDGE,"E42"),sQuery(id+"F0.wireOp",EDGE,"E43"),sQuery(id+"F0.wireOp",EDGE,"E44"),sQuery(id+"F0.wireOp",EDGE,"E45"),sQuery(id+"F0.wireOp",EDGE,"E46"),sQuery(id+"F0.wireOp",EDGE,"E47"),sQuery(id+"F0.wireOp",EDGE,"E48"),sQuery(id+"F0.wireOp",EDGE,"E49"),sQuery(id+"F0.wireOp",EDGE,"E50"),sQuery(id+"F0.wireOp",EDGE,"E51"),sQuery(id+"F0.wireOp",EDGE,"E52"),sQuery(id+"F0.wireOp",EDGE,"E53"),sQuery(id+"F0.wireOp",EDGE,"E54"),sQuery(id+"F0.wireOp",EDGE,"E55"),sQuery(id+"F0.wireOp",EDGE,"E56"),sQuery(id+"F0.wireOp",EDGE,"E57"),sQuery(id+"F0.wireOp",EDGE,"E58"),sQuery(id+"F0.wireOp",EDGE,"E59"),sQuery(id+"F0.wireOp",EDGE,"E60"),sQuery(id+"F0.wireOp",EDGE,"E61"),sQuery(id+"F0.wireOp",EDGE,"E62"),sQuery(id+"F0.wireOp",EDGE,"E63"),sQuery(id+"F0.wireOp",EDGE,"E64"),sQuery(id+"F0.wireOp",EDGE,"E65"),sQuery(id+"F0.wireOp",EDGE,"E66"),sQuery(id+"F0.wireOp",EDGE,"E67"),sQuery(id+"F0.wireOp",EDGE,"E68"),sQuery(id+"F0.wireOp",EDGE,"E69"),sQuery(id+"F0.wireOp",EDGE,"E70"),sQuery(id+"F0.wireOp",EDGE,"E71"),sQuery(id+"F0.wireOp",EDGE,"E72"),sQuery(id+"F0.wireOp",EDGE,"E73"),sQuery(id+"F0.wireOp",EDGE,"E74"),sQuery(id+"F0.wireOp",EDGE,"E75"),sQuery(id+"F0.wireOp",EDGE,"E76"),sQuery(id+"F0.wireOp",EDGE,"E77"),sQuery(id+"F0.wireOp",EDGE,"E78"),sQuery(id+"F0.wireOp",EDGE,"E79"),sQuery(id+"F0.wireOp",EDGE,"E80"),sQuery(id+"F0.wireOp",EDGE,"E81"),sQuery(id+"F0.wireOp",EDGE,"E82"),sQuery(id+"F0.wireOp",EDGE,"E83"),sQuery(id+"F0.wireOp",EDGE,"E84"),sQuery(id+"F0.wireOp",EDGE,"E85"),sQuery(id+"F0.wireOp",EDGE,"E86"),sQuery(id+"F0.wireOp",EDGE,"E87"),sQuery(id+"F0.wireOp",EDGE,"E88"),sQuery(id+"F0.wireOp",EDGE,"E89"),sQuery(id+"F0.wireOp",EDGE,"E90"),sQuery(id+"F0.wireOp",EDGE,"E91"),sQuery(id+"F0.wireOp",EDGE,"E92"),sQuery(id+"F0.wireOp",EDGE,"E93"),sQuery(id+"F0.wireOp",EDGE,"E94"),sQuery(id+"F0.wireOp",EDGE,"E95"),sQuery(id+"F0.wireOp",EDGE,"E96"),sQuery(id+"F0.wireOp",EDGE,"E97"),sQuery(id+"F0.wireOp",EDGE,"E98"),sQuery(id+"F0.wireOp",EDGE,"E99"),sQuery(id+"F0.wireOp",EDGE,"E100"),sQuery(id+"F0.wireOp",EDGE,"E101"),sQuery(id+"F0.wireOp",EDGE,"E102"),sQuery(id+"F0.wireOp",EDGE,"E103"),sQuery(id+"F0.wireOp",EDGE,"E104"),sQuery(id+"F0.wireOp",EDGE,"E105"),sQuery(id+"F0.wireOp",EDGE,"E106"),sQuery(id+"F0.wireOp",EDGE,"E107"),sQuery(id+"F0.wireOp",EDGE,"E108"),sQuery(id+"F0.wireOp",EDGE,"E109"),sQuery(id+"F0.wireOp",EDGE,"E110"),sQuery(id+"F0.wireOp",EDGE,"E111"),sQuery(id+"F0.wireOp",EDGE,"E112"),sQuery(id+"F0.wireOp",EDGE,"E113"),sQuery(id+"F0.wireOp",EDGE,"E114"),sQuery(id+"F0.wireOp",EDGE,"E115"),sQuery(id+"F0.wireOp",EDGE,"E116"),sQuery(id+"F0.wireOp",EDGE,"E117"),sQuery(id+"F0.wireOp",EDGE,"E118"),sQuery(id+"F0.wireOp",EDGE,"E119"),sQuery(id+"F0.wireOp",EDGE,"E120"),sQuery(id+"F0.wireOp",EDGE,"E121"),sQuery(id+"F0.wireOp",EDGE,"E122"),sQuery(id+"F0.wireOp",EDGE,"E123"),sQuery(id+"F0.wireOp",EDGE,"E124"),sQuery(id+"F0.wireOp",EDGE,"E125"),sQuery(id+"F0.wireOp",EDGE,"E126"),sQuery(id+"F0.wireOp",EDGE,"E127"),sQuery(id+"F0.wireOp",EDGE,"E128"),sQuery(id+"F0.wireOp",EDGE,"E129"),sQuery(id+"F0.wireOp",EDGE,"E130"),sQuery(id+"F0.wireOp",EDGE,"E131"),sQuery(id+"F0.wireOp",EDGE,"E132"),sQuery(id+"F0.wireOp",EDGE,"E133"),sQuery(id+"F0.wireOp",EDGE,"E134"),sQuery(id+"F0.wireOp",EDGE,"E135"),sQuery(id+"F0.wireOp",EDGE,"E136"),sQuery(id+"F0.wireOp",EDGE,"E137"),sQuery(id+"F0.wireOp",EDGE,"E138"),sQuery(id+"F0.wireOp",EDGE,"E139"),sQuery(id+"F0.wireOp",EDGE,"E140"),sQuery(id+"F0.wireOp",EDGE,"E141"),sQuery(id+"F0.wireOp",EDGE,"E142"),sQuery(id+"F0.wireOp",EDGE,"E143"),sQuery(id+"F0.wireOp",EDGE,"E144"),sQuery(id+"F0.wireOp",EDGE,"E145"),sQuery(id+"F0.wireOp",EDGE,"E146"),sQuery(id+"F0.wireOp",EDGE,"E147"),sQuery(id+"F0.wireOp",EDGE,"E148"),sQuery(id+"F0.wireOp",EDGE,"E149"),sQuery(id+"F0.wireOp",EDGE,"E150"),sQuery(id+"F0.wireOp",EDGE,"E151"),sQuery(id+"F0.wireOp",EDGE,"E152"),sQuery(id+"F0.wireOp",EDGE,"E153"),sQuery(id+"F0.wireOp",EDGE,"E154"),sQuery(id+"F0.wireOp",EDGE,"E155"),sQuery(id+"F0.wireOp",EDGE,"E156"),sQuery(id+"F0.wireOp",EDGE,"E157"),sQuery(id+"F0.wireOp",EDGE,"E158"),sQuery(id+"F0.wireOp",EDGE,"E159"),sQuery(id+"F0.wireOp",EDGE,"E160"),sQuery(id+"F0.wireOp",EDGE,"E161"),sQuery(id+"F0.wireOp",EDGE,"E162"),sQuery(id+"F0.wireOp",EDGE,"E163"),sQuery(id+"F0.wireOp",EDGE,"E164"),sQuery(id+"F0.wireOp",EDGE,"E165"),sQuery(id+"F0.wireOp",EDGE,"E166"),sQuery(id+"F0.wireOp",EDGE,"E167"),sQuery(id+"F0.wireOp",EDGE,"E168"),sQuery(id+"F0.wireOp",EDGE,"E169"),sQuery(id+"F0.wireOp",EDGE,"E170"),sQuery(id+"F0.wireOp",EDGE,"E171"),sQuery(id+"F0.wireOp",EDGE,"E172"),sQuery(id+"F0.wireOp",EDGE,"E173"),sQuery(id+"F0.wireOp",EDGE,"E174"),sQuery(id+"F0.wireOp",EDGE,"E175"),sQuery(id+"F0.wireOp",EDGE,"E176"),sQuery(id+"F0.wireOp",EDGE,"E177"),sQuery(id+"F0.wireOp",EDGE,"E178"),sQuery(id+"F0.wireOp",EDGE,"E179"),sQuery(id+"F0.wireOp",EDGE,"E180"),sQuery(id+"F0.wireOp",EDGE,"E181"),sQuery(id+"F0.wireOp",EDGE,"E182"),sQuery(id+"F0.wireOp",EDGE,"E183"),sQuery(id+"F0.wireOp",EDGE,"E184"),sQuery(id+"F0.wireOp",EDGE,"E185"),sQuery(id+"F0.wireOp",EDGE,"E186"),sQuery(id+"F0.wireOp",EDGE,"E187"),sQuery(id+"F0.wireOp",EDGE,"E188"),sQuery(id+"F0.wireOp",EDGE,"E189"),sQuery(id+"F0.wireOp",EDGE,"E190"),sQuery(id+"F0.wireOp",EDGE,"E191"),sQuery(id+"F0.wireOp",EDGE,"E192"),sQuery(id+"F0.wireOp",EDGE,"E193"),sQuery(id+"F0.wireOp",EDGE,"E194"),sQuery(id+"F0.wireOp",EDGE,"E195"),sQuery(id+"F0.wireOp",EDGE,"E196"),sQuery(id+"F0.wireOp",EDGE,"E197"),sQuery(id+"F0.wireOp",EDGE,"E198"),sQuery(id+"F0.wireOp",EDGE,"E199"),sQuery(id+"F0.wireOp",EDGE,"E200"),sQuery(id+"F0.wireOp",EDGE,"E201"),sQuery(id+"F0.wireOp",EDGE,"E202"),sQuery(id+"F0.wireOp",EDGE,"E203"),sQuery(id+"F0.wireOp",EDGE,"E204"),sQuery(id+"F0.wireOp",EDGE,"E205"),sQuery(id+"F0.wireOp",EDGE,"E206"),sQuery(id+"F0.wireOp",EDGE,"E207"),sQuery(id+"F0.wireOp",EDGE,"E208"),sQuery(id+"F0.wireOp",EDGE,"E209"),sQuery(id+"F0.wireOp",EDGE,"E210"),sQuery(id+"F0.wireOp",EDGE,"E211"),sQuery(id+"F0.wireOp",EDGE,"E212"),sQuery(id+"F0.wireOp",EDGE,"E213"),sQuery(id+"F0.wireOp",EDGE,"E214"),sQuery(id+"F0.wireOp",EDGE,"E215"),sQuery(id+"F0.wireOp",EDGE,"E216"),sQuery(id+"F0.wireOp",EDGE,"E217"),sQuery(id+"F0.wireOp",EDGE,"E218"),sQuery(id+"F0.wireOp",EDGE,"E219"),sQuery(id+"F0.wireOp",EDGE,"E220"),sQuery(id+"F0.wireOp",EDGE,"E221"),sQuery(id+"F0.wireOp",EDGE,"E222"),sQuery(id+"F0.wireOp",EDGE,"E223"),sQuery(id+"F0.wireOp",EDGE,"E224"),sQuery(id+"F0.wireOp",EDGE,"E225")])]});
            transform(context, id + "F9", {"entities" : qUnion([Q0]), "transformType" : TransformType.TRANSLATION_3D, "dx" : -44.33 * mm, "dy" : 0 * mm, "dz" : 39.02 * mm, "makeCopy" : false});
        }
        {
            var Q0;
            Q0=makeQuery(id+"F5.opExtrude","SWEPT_BODY",BODY,{"disambiguationData":[OSD([sQuery(id+"F4.wireOp",EDGE,"E226"),sQuery(id+"F4.wireOp",EDGE,"E227"),sQuery(id+"F4.wireOp",EDGE,"E228"),sQuery(id+"F4.wireOp",EDGE,"E229"),sQuery(id+"F4.wireOp",EDGE,"E230"),sQuery(id+"F4.wireOp",EDGE,"E231")])]});
            var Q1;
            Q1=makeQuery(id+"F5.opExtrude","SWEPT_BODY",BODY,{"disambiguationData":[OSD([sQuery(id+"F4.wireOp",EDGE,"E232"),sQuery(id+"F4.wireOp",EDGE,"E233"),sQuery(id+"F4.wireOp",EDGE,"E234"),sQuery(id+"F4.wireOp",EDGE,"E235"),sQuery(id+"F4.wireOp",EDGE,"E236"),sQuery(id+"F4.wireOp",EDGE,"E237"),sQuery(id+"F4.wireOp",EDGE,"E238"),sQuery(id+"F4.wireOp",EDGE,"E239"),sQuery(id+"F4.wireOp",EDGE,"E240"),sQuery(id+"F4.wireOp",EDGE,"E241"),sQuery(id+"F4.wireOp",EDGE,"E242"),sQuery(id+"F4.wireOp",EDGE,"E243")])]});
            var Q2;
            Q2=makeQuery(id+"F5.opExtrude","SWEPT_BODY",BODY,{"disambiguationData":[OSD([sQuery(id+"F4.wireOp",EDGE,"E244"),sQuery(id+"F4.wireOp",EDGE,"E245"),sQuery(id+"F4.wireOp",EDGE,"E246"),sQuery(id+"F4.wireOp",EDGE,"E247"),sQuery(id+"F4.wireOp",EDGE,"E248"),sQuery(id+"F4.wireOp",EDGE,"E249"),sQuery(id+"F4.wireOp",EDGE,"E250"),sQuery(id+"F4.wireOp",EDGE,"E251"),sQuery(id+"F4.wireOp",EDGE,"E252"),sQuery(id+"F4.wireOp",EDGE,"E253"),sQuery(id+"F4.wireOp",EDGE,"E254"),sQuery(id+"F4.wireOp",EDGE,"E255"),sQuery(id+"F4.wireOp",EDGE,"E256"),sQuery(id+"F4.wireOp",EDGE,"E257")])]});
            var Q3;
            Q3=makeQuery(id+"F5.opExtrude","SWEPT_BODY",BODY,{"disambiguationData":[OSD([sQuery(id+"F4.wireOp",EDGE,"E258"),sQuery(id+"F4.wireOp",EDGE,"E259"),sQuery(id+"F4.wireOp",EDGE,"E260"),sQuery(id+"F4.wireOp",EDGE,"E261")])]});
            var Q4;
            Q4=makeQuery(id+"F5.opExtrude","SWEPT_BODY",BODY,{"disambiguationData":[OSD([sQuery(id+"F4.wireOp",EDGE,"E262"),sQuery(id+"F4.wireOp",EDGE,"E263"),sQuery(id+"F4.wireOp",EDGE,"E264"),sQuery(id+"F4.wireOp",EDGE,"E265"),sQuery(id+"F4.wireOp",EDGE,"E266"),sQuery(id+"F4.wireOp",EDGE,"E267"),sQuery(id+"F4.wireOp",EDGE,"E268"),sQuery(id+"F4.wireOp",EDGE,"E269")])]});
            var Q5;
            Q5=makeQuery(id+"F5.opExtrude","SWEPT_BODY",BODY,{"disambiguationData":[OSD([sQuery(id+"F4.wireOp",EDGE,"E270"),sQuery(id+"F4.wireOp",EDGE,"E271"),sQuery(id+"F4.wireOp",EDGE,"E272"),sQuery(id+"F4.wireOp",EDGE,"E273"),sQuery(id+"F4.wireOp",EDGE,"E274"),sQuery(id+"F4.wireOp",EDGE,"E275"),sQuery(id+"F4.wireOp",EDGE,"E276"),sQuery(id+"F4.wireOp",EDGE,"E277"),sQuery(id+"F4.wireOp",EDGE,"E278"),sQuery(id+"F4.wireOp",EDGE,"E279"),sQuery(id+"F4.wireOp",EDGE,"E280"),sQuery(id+"F4.wireOp",EDGE,"E281")])]});
            var Q6;
            Q6=makeQuery(id+"F5.opExtrude","SWEPT_BODY",BODY,{"disambiguationData":[OSD([sQuery(id+"F4.wireOp",EDGE,"E282"),sQuery(id+"F4.wireOp",EDGE,"E283"),sQuery(id+"F4.wireOp",EDGE,"E284"),sQuery(id+"F4.wireOp",EDGE,"E285"),sQuery(id+"F4.wireOp",EDGE,"E286"),sQuery(id+"F4.wireOp",EDGE,"E287"),sQuery(id+"F4.wireOp",EDGE,"E288"),sQuery(id+"F4.wireOp",EDGE,"E289")])]});
            var Q7;
            Q7=makeQuery(id+"F5.opExtrude","SWEPT_BODY",BODY,{"disambiguationData":[OSD([sQuery(id+"F4.wireOp",EDGE,"E290"),sQuery(id+"F4.wireOp",EDGE,"E291"),sQuery(id+"F4.wireOp",EDGE,"E292"),sQuery(id+"F4.wireOp",EDGE,"E293"),sQuery(id+"F4.wireOp",EDGE,"E294"),sQuery(id+"F4.wireOp",EDGE,"E295"),sQuery(id+"F4.wireOp",EDGE,"E296"),sQuery(id+"F4.wireOp",EDGE,"E297")])]});
            var Q8;
            Q8=makeQuery(id+"F5.opExtrude","SWEPT_BODY",BODY,{"disambiguationData":[OSD([sQuery(id+"F4.wireOp",EDGE,"E298"),sQuery(id+"F4.wireOp",EDGE,"E299"),sQuery(id+"F4.wireOp",EDGE,"E300"),sQuery(id+"F4.wireOp",EDGE,"E301"),sQuery(id+"F4.wireOp",EDGE,"E302"),sQuery(id+"F4.wireOp",EDGE,"E303"),sQuery(id+"F4.wireOp",EDGE,"E304"),sQuery(id+"F4.wireOp",EDGE,"E305"),sQuery(id+"F4.wireOp",EDGE,"E306"),sQuery(id+"F4.wireOp",EDGE,"E307"),sQuery(id+"F4.wireOp",EDGE,"E308"),sQuery(id+"F4.wireOp",EDGE,"E309")])]});
            var Q9;
            Q9=makeQuery(id+"F5.opExtrude","SWEPT_BODY",BODY,{"disambiguationData":[OSD([sQuery(id+"F4.wireOp",EDGE,"E310"),sQuery(id+"F4.wireOp",EDGE,"E311"),sQuery(id+"F4.wireOp",EDGE,"E312"),sQuery(id+"F4.wireOp",EDGE,"E313"),sQuery(id+"F4.wireOp",EDGE,"E314"),sQuery(id+"F4.wireOp",EDGE,"E315")])]});
            var Q10;
            Q10=makeQuery(id+"F5.opExtrude","SWEPT_BODY",BODY,{"disambiguationData":[OSD([sQuery(id+"F4.wireOp",EDGE,"E316"),sQuery(id+"F4.wireOp",EDGE,"E317"),sQuery(id+"F4.wireOp",EDGE,"E318"),sQuery(id+"F4.wireOp",EDGE,"E319")])]});
            var Q11;
            Q11=makeQuery(id+"F5.opExtrude","SWEPT_BODY",BODY,{"disambiguationData":[OSD([sQuery(id+"F4.wireOp",EDGE,"E320"),sQuery(id+"F4.wireOp",EDGE,"E321"),sQuery(id+"F4.wireOp",EDGE,"E322"),sQuery(id+"F4.wireOp",EDGE,"E323"),sQuery(id+"F4.wireOp",EDGE,"E324"),sQuery(id+"F4.wireOp",EDGE,"E325"),sQuery(id+"F4.wireOp",EDGE,"E326"),sQuery(id+"F4.wireOp",EDGE,"E327"),sQuery(id+"F4.wireOp",EDGE,"E328"),sQuery(id+"F4.wireOp",EDGE,"E329"),sQuery(id+"F4.wireOp",EDGE,"E330"),sQuery(id+"F4.wireOp",EDGE,"E331")])]});
            transform(context, id + "F10", {"entities" : qUnion([Q0, Q1, Q2, Q3, Q4, Q5, Q6, Q7, Q8, Q9, Q10, Q11]), "transformType" : TransformType.TRANSLATION_3D, "dx" : -54.73 * mm, "dy" : 0 * mm, "dz" : -38.33 * mm, "makeCopy" : false});
        }
        {
            var Q0;
            Q0=makeQuery(id+"F5.opExtrude","CAP_FACE",FACE,{"disambiguationData":[OSD([sQuery(id+"F4.wireOp",EDGE,"E226"),sQuery(id+"F4.wireOp",EDGE,"E227"),sQuery(id+"F4.wireOp",EDGE,"E228"),sQuery(id+"F4.wireOp",EDGE,"E229"),sQuery(id+"F4.wireOp",EDGE,"E230"),sQuery(id+"F4.wireOp",EDGE,"E231")])],"isStart":false});
            extrude(context, id + "F11", {"entities" : qUnion([Q0]), "operationType" : NewBodyOperationType.REMOVE, "oppositeDirection" : true, "depth" : 25.4 * mm});
        }
        {
            var Q0;
            Q0=makeQuery(id+"F5.opExtrude","CAP_FACE",FACE,{"disambiguationData":[OSD([sQuery(id+"F4.wireOp",EDGE,"E232"),sQuery(id+"F4.wireOp",EDGE,"E233"),sQuery(id+"F4.wireOp",EDGE,"E234"),sQuery(id+"F4.wireOp",EDGE,"E235"),sQuery(id+"F4.wireOp",EDGE,"E236"),sQuery(id+"F4.wireOp",EDGE,"E237"),sQuery(id+"F4.wireOp",EDGE,"E238"),sQuery(id+"F4.wireOp",EDGE,"E239"),sQuery(id+"F4.wireOp",EDGE,"E240"),sQuery(id+"F4.wireOp",EDGE,"E241"),sQuery(id+"F4.wireOp",EDGE,"E242"),sQuery(id+"F4.wireOp",EDGE,"E243")])],"isStart":false});
            extrude(context, id + "F12", {"entities" : qUnion([Q0]), "operationType" : NewBodyOperationType.REMOVE, "oppositeDirection" : true, "depth" : 25.4 * mm});
        }
        {
            var Q0;
            Q0=makeQuery(id+"F5.opExtrude","CAP_FACE",FACE,{"disambiguationData":[OSD([sQuery(id+"F4.wireOp",EDGE,"E282"),sQuery(id+"F4.wireOp",EDGE,"E283"),sQuery(id+"F4.wireOp",EDGE,"E284"),sQuery(id+"F4.wireOp",EDGE,"E285"),sQuery(id+"F4.wireOp",EDGE,"E286"),sQuery(id+"F4.wireOp",EDGE,"E287"),sQuery(id+"F4.wireOp",EDGE,"E288"),sQuery(id+"F4.wireOp",EDGE,"E289")])],"isStart":false});
            extrude(context, id + "F13", {"entities" : qUnion([Q0]), "operationType" : NewBodyOperationType.REMOVE, "oppositeDirection" : true, "depth" : 25.4 * mm});
        }
        {
            var Q0;
            Q0=makeQuery(id+"F5.opExtrude","CAP_FACE",FACE,{"disambiguationData":[OSD([sQuery(id+"F4.wireOp",EDGE,"E290"),sQuery(id+"F4.wireOp",EDGE,"E291"),sQuery(id+"F4.wireOp",EDGE,"E292"),sQuery(id+"F4.wireOp",EDGE,"E293"),sQuery(id+"F4.wireOp",EDGE,"E294"),sQuery(id+"F4.wireOp",EDGE,"E295"),sQuery(id+"F4.wireOp",EDGE,"E296"),sQuery(id+"F4.wireOp",EDGE,"E297")])],"isStart":false});
            extrude(context, id + "F14", {"entities" : qUnion([Q0]), "operationType" : NewBodyOperationType.REMOVE, "oppositeDirection" : true, "depth" : 25.4 * mm});
        }
        {
            var Q0;
            Q0=makeQuery(id+"F5.opExtrude","CAP_FACE",FACE,{"disambiguationData":[OSD([sQuery(id+"F4.wireOp",EDGE,"E244"),sQuery(id+"F4.wireOp",EDGE,"E245"),sQuery(id+"F4.wireOp",EDGE,"E246"),sQuery(id+"F4.wireOp",EDGE,"E247"),sQuery(id+"F4.wireOp",EDGE,"E248"),sQuery(id+"F4.wireOp",EDGE,"E249"),sQuery(id+"F4.wireOp",EDGE,"E250"),sQuery(id+"F4.wireOp",EDGE,"E251"),sQuery(id+"F4.wireOp",EDGE,"E252"),sQuery(id+"F4.wireOp",EDGE,"E253"),sQuery(id+"F4.wireOp",EDGE,"E254"),sQuery(id+"F4.wireOp",EDGE,"E255"),sQuery(id+"F4.wireOp",EDGE,"E256"),sQuery(id+"F4.wireOp",EDGE,"E257")])],"isStart":false});
            extrude(context, id + "F15", {"entities" : qUnion([Q0]), "operationType" : NewBodyOperationType.REMOVE, "oppositeDirection" : true, "depth" : 25.4 * mm});
        }
        {
            var Q0;
            Q0=makeQuery(id+"F5.opExtrude","CAP_FACE",FACE,{"disambiguationData":[OSD([sQuery(id+"F4.wireOp",EDGE,"E258"),sQuery(id+"F4.wireOp",EDGE,"E259"),sQuery(id+"F4.wireOp",EDGE,"E260"),sQuery(id+"F4.wireOp",EDGE,"E261")])],"isStart":false});
            extrude(context, id + "F16", {"entities" : qUnion([Q0]), "operationType" : NewBodyOperationType.REMOVE, "oppositeDirection" : true, "depth" : 25.4 * mm});
        }
        {
            var Q0;
            Q0=makeQuery(id+"F5.opExtrude","CAP_FACE",FACE,{"disambiguationData":[OSD([sQuery(id+"F4.wireOp",EDGE,"E262"),sQuery(id+"F4.wireOp",EDGE,"E263"),sQuery(id+"F4.wireOp",EDGE,"E264"),sQuery(id+"F4.wireOp",EDGE,"E265"),sQuery(id+"F4.wireOp",EDGE,"E266"),sQuery(id+"F4.wireOp",EDGE,"E267"),sQuery(id+"F4.wireOp",EDGE,"E268"),sQuery(id+"F4.wireOp",EDGE,"E269")])],"isStart":false});
            extrude(context, id + "F17", {"entities" : qUnion([Q0]), "operationType" : NewBodyOperationType.REMOVE, "oppositeDirection" : true, "depth" : 25.4 * mm});
        }
        {
            var Q0;
            Q0=makeQuery(id+"F5.opExtrude","CAP_FACE",FACE,{"disambiguationData":[OSD([sQuery(id+"F4.wireOp",EDGE,"E270"),sQuery(id+"F4.wireOp",EDGE,"E271"),sQuery(id+"F4.wireOp",EDGE,"E272"),sQuery(id+"F4.wireOp",EDGE,"E273"),sQuery(id+"F4.wireOp",EDGE,"E274"),sQuery(id+"F4.wireOp",EDGE,"E275"),sQuery(id+"F4.wireOp",EDGE,"E276"),sQuery(id+"F4.wireOp",EDGE,"E277"),sQuery(id+"F4.wireOp",EDGE,"E278"),sQuery(id+"F4.wireOp",EDGE,"E279"),sQuery(id+"F4.wireOp",EDGE,"E280"),sQuery(id+"F4.wireOp",EDGE,"E281")])],"isStart":false});
            extrude(context, id + "F18", {"entities" : qUnion([Q0]), "operationType" : NewBodyOperationType.REMOVE, "oppositeDirection" : true, "depth" : 25.4 * mm});
        }
        {
            var Q0;
            Q0=makeQuery(id+"F5.opExtrude","CAP_FACE",FACE,{"disambiguationData":[OSD([sQuery(id+"F4.wireOp",EDGE,"E298"),sQuery(id+"F4.wireOp",EDGE,"E299"),sQuery(id+"F4.wireOp",EDGE,"E300"),sQuery(id+"F4.wireOp",EDGE,"E301"),sQuery(id+"F4.wireOp",EDGE,"E302"),sQuery(id+"F4.wireOp",EDGE,"E303"),sQuery(id+"F4.wireOp",EDGE,"E304"),sQuery(id+"F4.wireOp",EDGE,"E305"),sQuery(id+"F4.wireOp",EDGE,"E306"),sQuery(id+"F4.wireOp",EDGE,"E307"),sQuery(id+"F4.wireOp",EDGE,"E308"),sQuery(id+"F4.wireOp",EDGE,"E309")])],"isStart":false});
            extrude(context, id + "F19", {"entities" : qUnion([Q0]), "operationType" : NewBodyOperationType.REMOVE, "oppositeDirection" : true, "depth" : 25.4 * mm});
        }
        {
            var Q0;
            Q0=makeQuery(id+"F5.opExtrude","CAP_FACE",FACE,{"disambiguationData":[OSD([sQuery(id+"F4.wireOp",EDGE,"E310"),sQuery(id+"F4.wireOp",EDGE,"E311"),sQuery(id+"F4.wireOp",EDGE,"E312"),sQuery(id+"F4.wireOp",EDGE,"E313"),sQuery(id+"F4.wireOp",EDGE,"E314"),sQuery(id+"F4.wireOp",EDGE,"E315")])],"isStart":false});
            extrude(context, id + "F20", {"entities" : qUnion([Q0]), "operationType" : NewBodyOperationType.REMOVE, "oppositeDirection" : true, "depth" : 25.4 * mm});
        }
        {
            var Q0;
            Q0=makeQuery(id+"F5.opExtrude","CAP_FACE",FACE,{"disambiguationData":[OSD([sQuery(id+"F4.wireOp",EDGE,"E316"),sQuery(id+"F4.wireOp",EDGE,"E317"),sQuery(id+"F4.wireOp",EDGE,"E318"),sQuery(id+"F4.wireOp",EDGE,"E319")])],"isStart":false});
            extrude(context, id + "F21", {"entities" : qUnion([Q0]), "operationType" : NewBodyOperationType.REMOVE, "oppositeDirection" : true, "depth" : 25.4 * mm});
        }
        {
            var Q0;
            Q0=makeQuery(id+"F5.opExtrude","CAP_FACE",FACE,{"disambiguationData":[OSD([sQuery(id+"F4.wireOp",EDGE,"E320"),sQuery(id+"F4.wireOp",EDGE,"E321"),sQuery(id+"F4.wireOp",EDGE,"E322"),sQuery(id+"F4.wireOp",EDGE,"E323"),sQuery(id+"F4.wireOp",EDGE,"E324"),sQuery(id+"F4.wireOp",EDGE,"E325"),sQuery(id+"F4.wireOp",EDGE,"E326"),sQuery(id+"F4.wireOp",EDGE,"E327"),sQuery(id+"F4.wireOp",EDGE,"E328"),sQuery(id+"F4.wireOp",EDGE,"E329"),sQuery(id+"F4.wireOp",EDGE,"E330"),sQuery(id+"F4.wireOp",EDGE,"E331")])],"isStart":false});
            extrude(context, id + "F22", {"entities" : qUnion([Q0]), "operationType" : NewBodyOperationType.REMOVE, "oppositeDirection" : true, "depth" : 25.4 * mm});
        }
        {
            var Q0;
            Q0=qCreatedBy(makeId("Front.planeOp"),FACE);
            var sketch = newSketch(context, id + "F23", { "sketchPlane" : qUnion([Q0])});
            skCircle(sketch, "E332", {"center": v(20.45, 49.76) * mm, "radius": 3.58 * mm});
            skSolve(sketch);
        }
        {
            var Q0;
            Q0=makeQuery(id+"F23.imprint","IMPRINT",FACE,{"disambiguationData":[TD([[makeQuery(id+"F23.imprint","IMPRINT",EDGE,{"derivedFrom":sQuery(id+"F23.wireOp",EDGE,"E332")}),1.0]])]});
            extrude(context, id + "F24", {"entities" : qUnion([Q0]), "depth" : 25.4 * mm});
        }
        {
            var Q0;
            Q0=makeQuery(id+"F24.opExtrude","SWEPT_BODY",BODY,{"disambiguationData":[OSD([sQuery(id+"F23.wireOp",EDGE,"E332")])]});
            transform(context, id + "F25", {"entities" : qUnion([Q0]), "transformType" : TransformType.TRANSLATION_3D, "dx" : -76.43 * mm, "dy" : 0 * mm, "dz" : -0.7 * mm, "makeCopy" : false});
        }
        {
            var Q0;
            Q0=makeQuery(id+"F24.opExtrude","CAP_FACE",FACE,{"disambiguationData":[OSD([sQuery(id+"F23.wireOp",EDGE,"E332")])],"isStart":true});
            extrude(context, id + "F26", {"entities" : qUnion([Q0]), "operationType" : NewBodyOperationType.REMOVE, "oppositeDirection" : true, "depth" : 46.95 * mm});
        }
    });
